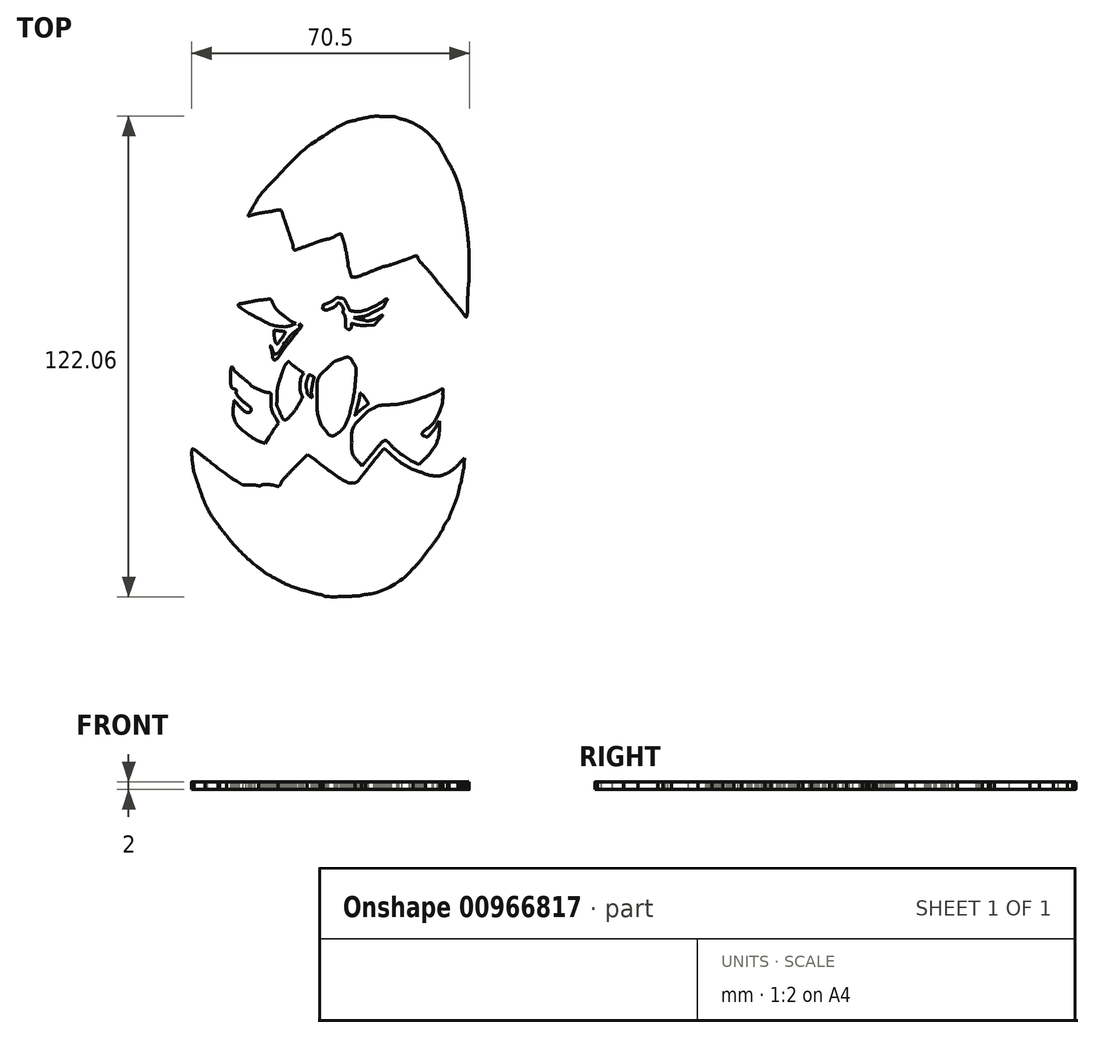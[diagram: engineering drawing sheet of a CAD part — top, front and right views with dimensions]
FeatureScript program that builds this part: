
annotation { "Feature Type Name" : "Feature", "Feature Type Description" : "" }
export const myFeature = defineFeature(function(context is Context, id is Id, definition is map)
    precondition{}
    {
        {
            var Q0;
            Q0=qCreatedBy(makeId("Top.planeOp"),FACE);
            var sketch = newSketch(context, id + "F0", { "sketchPlane" : qUnion([Q0])});
            skLineSegment(sketch, "E0", {"start": v(-17.46, -21.76) * mm, "end": v(-17.2, -21.16) * mm});
            skLineSegment(sketch, "E1", {"start": v(-17.2, -21.16) * mm, "end": v(-18.13, -20.78) * mm});
            skLineSegment(sketch, "E2", {"start": v(-18.45, 30) * mm, "end": v(-17.65, 29.34) * mm});
            skLineSegment(sketch, "E3", {"start": v(-17.65, 29.34) * mm, "end": v(-16.71, 30.75) * mm});
            skLineSegment(sketch, "E4", {"start": v(1.27, -59.92) * mm, "end": v(1.27, -59.92) * mm});
            skLineSegment(sketch, "E5", {"start": v(34.2, -24.61) * mm, "end": v(34.3, -23.27) * mm});
            skLineSegment(sketch, "E6", {"start": v(34.3, -23.27) * mm, "end": v(33.3, -24.29) * mm});
            skLineSegment(sketch, "E7", {"start": v(-3.64, -23.79) * mm, "end": v(-5.61, -22.3) * mm});
            skLineSegment(sketch, "E8", {"start": v(-5.61, -22.3) * mm, "end": v(-8.8, -25.56) * mm});
            skLineSegment(sketch, "E9", {"start": v(-20.36, -30.12) * mm, "end": v(-22.08, -30.1) * mm});
            skLineSegment(sketch, "E10", {"start": v(-22.08, -30.1) * mm, "end": v(-23.62, -29.13) * mm});
            skLineSegment(sketch, "E11", {"start": v(-17.15, -27.15) * mm, "end": v(-17.23, -28.47) * mm});
            skLineSegment(sketch, "E12", {"start": v(-17.23, -28.47) * mm, "end": v(-16.05, -28.52) * mm});
            skLineSegment(sketch, "E13", {"start": v(22.12, -24.58) * mm, "end": v(22.75, -24.87) * mm});
            skLineSegment(sketch, "E14", {"start": v(22.75, -24.87) * mm, "end": v(24.01, -23.63) * mm});
            skLineSegment(sketch, "E15", {"start": v(27.87, -15.36) * mm, "end": v(27.96, -13.82) * mm});
            skLineSegment(sketch, "E16", {"start": v(27.96, -13.82) * mm, "end": v(27.27, -14.85) * mm});
            skLineSegment(sketch, "E17", {"start": v(7.53, -24.44) * mm, "end": v(8.27, -25.28) * mm});
            skLineSegment(sketch, "E18", {"start": v(8.27, -25.28) * mm, "end": v(8.8, -24.62) * mm});
            skLineSegment(sketch, "E19", {"start": v(-13.66, -15.29) * mm, "end": v(-12.95, -14.31) * mm});
            skLineSegment(sketch, "E20", {"start": v(-12.95, -14.31) * mm, "end": v(-13.44, -13.47) * mm});
            skLineSegment(sketch, "E21", {"start": v(-17.02, -19.32) * mm, "end": v(-16.43, -19.53) * mm});
            skLineSegment(sketch, "E22", {"start": v(-16.43, -19.53) * mm, "end": v(-15.4, -17.9) * mm});
            skLineSegment(sketch, "E23", {"start": v(-6.81, -2.07) * mm, "end": v(-6.57, -1.6) * mm});
            skLineSegment(sketch, "E24", {"start": v(-6.57, -1.6) * mm, "end": v(-7.92, -0.7) * mm});
            skLineSegment(sketch, "E25", {"start": v(29.38, 15.62) * mm, "end": v(29.62, 16.5) * mm});
            skLineSegment(sketch, "E26", {"start": v(29.62, 16.5) * mm, "end": v(28.6, 17.81) * mm});
            skLineSegment(sketch, "E27", {"start": v(2.14, 31.23) * mm, "end": v(1.95, 31.69) * mm});
            skLineSegment(sketch, "E28", {"start": v(1.95, 31.69) * mm, "end": v(1.17, 31.38) * mm});
            skLineSegment(sketch, "E29", {"start": v(-14.7, 31.12) * mm, "end": v(-15.85, 29.58) * mm});
            skLineSegment(sketch, "E30", {"start": v(-15.85, 29.58) * mm, "end": v(-15.28, 29.52) * mm});
            skLineSegment(sketch, "E31", {"start": v(-4.13, -0.77) * mm, "end": v(-3.33, -1.07) * mm});
            skLineSegment(sketch, "E32", {"start": v(-3.33, -1.07) * mm, "end": v(-1.73, 0.55) * mm});
            skLineSegment(sketch, "E33", {"start": v(10.62, -1.64) * mm, "end": v(10.62, -1.64) * mm});
            skLineSegment(sketch, "E34", {"start": v(7.22, 12.57) * mm, "end": v(6.1, 12.46) * mm});
            skLineSegment(sketch, "E35", {"start": v(6.1, 12.46) * mm, "end": v(6.76, 12.23) * mm});
            skLineSegment(sketch, "E36", {"start": v(11.8, 11.02) * mm, "end": v(11.39, 10.49) * mm});
            skLineSegment(sketch, "E37", {"start": v(11.39, 10.49) * mm, "end": v(9.4, 10.47) * mm});
            skLineSegment(sketch, "E38", {"start": v(-9.31, 10.68) * mm, "end": v(-8.56, 10.9) * mm});
            skLineSegment(sketch, "E39", {"start": v(-8.56, 10.9) * mm, "end": v(-9.36, 11.3) * mm});
            skFitSpline(sketch, "E40", {"points": [v(1.27, -59.92) * mm, v(1.26, -59.9) * mm, v(0.65, -59.88) * mm, v(-0.08, -59.86) * mm]});
            skFitSpline(sketch, "E41", {"points": [v(-0.08, -59.86) * mm, v(-1.27, -59.82) * mm, v(-3.66, -59.47) * mm, v(-3.97, -59.28) * mm]});
            skFitSpline(sketch, "E42", {"points": [v(-3.97, -59.28) * mm, v(-4.04, -59.24) * mm, v(-4.28, -59.17) * mm, v(-4.5, -59.13) * mm]});
            skFitSpline(sketch, "E43", {"points": [v(-4.5, -59.13) * mm, v(-4.74, -59.08) * mm, v(-5.43, -58.89) * mm, v(-6.04, -58.69) * mm]});
            skFitSpline(sketch, "E44", {"points": [v(-6.04, -58.69) * mm, v(-6.66, -58.49) * mm, v(-7.34, -58.29) * mm, v(-7.55, -58.25) * mm]});
            skFitSpline(sketch, "E45", {"points": [v(-7.55, -58.25) * mm, v(-7.95, -58.17) * mm, v(-9.79, -57.56) * mm, v(-10.41, -57.3) * mm]});
            skFitSpline(sketch, "E46", {"points": [v(-10.41, -57.3) * mm, v(-10.6, -57.23) * mm, v(-11.03, -57.06) * mm, v(-11.36, -56.95) * mm]});
            skFitSpline(sketch, "E47", {"points": [v(-11.36, -56.95) * mm, v(-12.67, -56.48) * mm, v(-16.33, -54.48) * mm, v(-17.73, -53.48) * mm]});
            skFitSpline(sketch, "E48", {"points": [v(-17.73, -53.48) * mm, v(-19.95, -51.87) * mm, v(-20.39, -51.49) * mm, v(-23.53, -48.3) * mm]});
            skFitSpline(sketch, "E49", {"points": [v(-23.53, -48.3) * mm, v(-26.57, -45.24) * mm, v(-27.3, -44.44) * mm, v(-27.3, -44.2) * mm]});
            skFitSpline(sketch, "E50", {"points": [v(-27.3, -44.2) * mm, v(-27.3, -44.13) * mm, v(-27.69, -43.67) * mm, v(-28.15, -43.18) * mm]});
            skFitSpline(sketch, "E51", {"points": [v(-28.15, -43.18) * mm, v(-29.6, -41.64) * mm, v(-32.25, -37.44) * mm, v(-33.3, -35) * mm]});
            skFitSpline(sketch, "E52", {"points": [v(-33.3, -35) * mm, v(-33.74, -33.98) * mm, v(-34.5, -31.98) * mm, v(-34.6, -31.57) * mm]});
            skFitSpline(sketch, "E53", {"points": [v(-34.6, -31.57) * mm, v(-34.63, -31.43) * mm, v(-34.87, -30.73) * mm, v(-35.12, -30.03) * mm]});
            skFitSpline(sketch, "E54", {"points": [v(-35.12, -30.03) * mm, v(-36.14, -27.15) * mm, v(-36.31, -26.07) * mm, v(-36.31, -22.74) * mm]});
            skFitSpline(sketch, "E55", {"points": [v(-36.31, -22.74) * mm, v(-36.31, -19.95) * mm, v(-36.16, -18.7) * mm, v(-35.78, -18.41) * mm]});
            skFitSpline(sketch, "E56", {"points": [v(-35.78, -18.41) * mm, v(-35.35, -18.1) * mm, v(-35.24, -18.13) * mm, v(-34.72, -18.68) * mm]});
            skFitSpline(sketch, "E57", {"points": [v(-34.72, -18.68) * mm, v(-34.46, -18.94) * mm, v(-33.4, -19.8) * mm, v(-32.37, -20.6) * mm]});
            skFitSpline(sketch, "E58", {"points": [v(-32.37, -20.6) * mm, v(-31.33, -21.4) * mm, v(-30.44, -22.08) * mm, v(-30.4, -22.13) * mm]});
            skFitSpline(sketch, "E59", {"points": [v(-30.4, -22.13) * mm, v(-30.35, -22.18) * mm, v(-30, -22.45) * mm, v(-29.62, -22.73) * mm]});
            skFitSpline(sketch, "E60", {"points": [v(-29.62, -22.73) * mm, v(-29.25, -23) * mm, v(-28.9, -23.28) * mm, v(-28.85, -23.34) * mm]});
            skFitSpline(sketch, "E61", {"points": [v(-28.85, -23.34) * mm, v(-28.5, -23.78) * mm, v(-24.34, -26.7) * mm, v(-21.83, -28.27) * mm]});
            skFitSpline(sketch, "E62", {"points": [v(-21.83, -28.27) * mm, v(-21.4, -28.54) * mm, v(-18.97, -28.72) * mm, v(-18.83, -28.5) * mm]});
            skFitSpline(sketch, "E63", {"points": [v(-18.83, -28.5) * mm, v(-18.8, -28.44) * mm, v(-18.71, -27.85) * mm, v(-18.66, -27.2) * mm]});
            skFitSpline(sketch, "E64", {"points": [v(-18.66, -27.2) * mm, v(-18.6, -26.53) * mm, v(-18.52, -25.88) * mm, v(-18.48, -25.74) * mm]});
            skFitSpline(sketch, "E65", {"points": [v(-18.48, -25.74) * mm, v(-18.44, -25.6) * mm, v(-18.36, -25.21) * mm, v(-18.3, -24.88) * mm]});
            skFitSpline(sketch, "E66", {"points": [v(-18.3, -24.88) * mm, v(-18.15, -23.95) * mm, v(-17.73, -22.42) * mm, v(-17.46, -21.76) * mm]});
            skFitSpline(sketch, "E67", {"points": [v(-18.13, -20.78) * mm, v(-19.25, -20.32) * mm, v(-21.1, -19.04) * mm, v(-22.2, -17.97) * mm]});
            skFitSpline(sketch, "E68", {"points": [v(-22.2, -17.97) * mm, v(-24.52, -15.7) * mm, v(-25.92, -12.27) * mm, v(-25.71, -9.36) * mm]});
            skFitSpline(sketch, "E69", {"points": [v(-25.71, -9.36) * mm, v(-25.66, -8.6) * mm, v(-25.57, -7.8) * mm, v(-25.52, -7.56) * mm]});
            skFitSpline(sketch, "E70", {"points": [v(-25.52, -7.56) * mm, v(-25.45, -7.28) * mm, v(-25.58, -6.8) * mm, v(-25.9, -6.19) * mm]});
            skFitSpline(sketch, "E71", {"points": [v(-25.9, -6.19) * mm, v(-26.36, -5.26) * mm, v(-26.36, -5.19) * mm, v(-26.34, -2.4) * mm]});
            skFitSpline(sketch, "E72", {"points": [v(-26.34, -2.4) * mm, v(-26.32, 0.35) * mm, v(-26.3, 0.5) * mm, v(-25.83, 1.5) * mm]});
            skFitSpline(sketch, "E73", {"points": [v(-25.83, 1.5) * mm, v(-25.31, 2.6) * mm, v(-25.08, 2.81) * mm, v(-24.52, 2.63) * mm]});
            skFitSpline(sketch, "E74", {"points": [v(-24.52, 2.63) * mm, v(-24.2, 2.53) * mm, v(-23.26, 0.76) * mm, v(-23.35, 0.42) * mm]});
            skFitSpline(sketch, "E75", {"points": [v(-23.35, 0.42) * mm, v(-23.37, 0.32) * mm, v(-23.34, 0.3) * mm, v(-23.28, 0.36) * mm]});
            skFitSpline(sketch, "E76", {"points": [v(-23.28, 0.36) * mm, v(-23.21, 0.43) * mm, v(-22.92, 0.2) * mm, v(-22.62, -0.15) * mm]});
            skFitSpline(sketch, "E77", {"points": [v(-22.62, -0.15) * mm, v(-21.35, -1.63) * mm, v(-19.86, -2.83) * mm, v(-18.05, -3.82) * mm]});
            skFitSpline(sketch, "E78", {"points": [v(-18.05, -3.82) * mm, v(-16.84, -4.48) * mm, v(-14.67, -5.27) * mm, v(-14.5, -5.1) * mm]});
            skFitSpline(sketch, "E79", {"points": [v(-14.5, -5.1) * mm, v(-14.45, -5.05) * mm, v(-14.34, -4.64) * mm, v(-14.25, -4.2) * mm]});
            skFitSpline(sketch, "E80", {"points": [v(-14.25, -4.2) * mm, v(-14.17, -3.75) * mm, v(-13.8, -2.54) * mm, v(-13.42, -1.51) * mm]});
            skFitSpline(sketch, "E81", {"points": [v(-13.42, -1.51) * mm, v(-13.04, -0.48) * mm, v(-12.73, 0.4) * mm, v(-12.73, 0.44) * mm]});
            skFitSpline(sketch, "E82", {"points": [v(-12.73, 0.44) * mm, v(-12.73, 0.48) * mm, v(-12.88, 0.44) * mm, v(-13.06, 0.34) * mm]});
            skFitSpline(sketch, "E83", {"points": [v(-13.06, 0.34) * mm, v(-13.52, 0.1) * mm, v(-14.64, 0.13) * mm, v(-15, 0.4) * mm]});
            skFitSpline(sketch, "E84", {"points": [v(-15, 0.4) * mm, v(-15.38, 0.69) * mm, v(-15.76, 1.59) * mm, v(-15.9, 2.56) * mm]});
            skFitSpline(sketch, "E85", {"points": [v(-15.9, 2.56) * mm, v(-15.96, 2.98) * mm, v(-16.08, 3.44) * mm, v(-16.15, 3.58) * mm]});
            skFitSpline(sketch, "E86", {"points": [v(-16.15, 3.58) * mm, v(-16.27, 3.82) * mm, v(-16.4, 4.35) * mm, v(-16.62, 5.56) * mm]});
            skFitSpline(sketch, "E87", {"points": [v(-16.62, 5.56) * mm, v(-16.66, 5.75) * mm, v(-16.76, 6.18) * mm, v(-16.84, 6.5) * mm]});
            skFitSpline(sketch, "E88", {"points": [v(-16.84, 6.5) * mm, v(-16.93, 6.84) * mm, v(-17.05, 7.5) * mm, v(-17.1, 7.96) * mm]});
            skFitSpline(sketch, "E89", {"points": [v(-17.1, 7.96) * mm, v(-17.34, 10) * mm, v(-17.42, 10.14) * mm, v(-18.96, 10.96) * mm]});
            skFitSpline(sketch, "E90", {"points": [v(-18.96, 10.96) * mm, v(-21.2, 12.16) * mm, v(-22.57, 13.1) * mm, v(-23.47, 14.06) * mm]});
            skFitSpline(sketch, "E91", {"points": [v(-23.47, 14.06) * mm, v(-23.93, 14.55) * mm, v(-24.56, 15.19) * mm, v(-24.86, 15.48) * mm]});
            skFitSpline(sketch, "E92", {"points": [v(-24.86, 15.48) * mm, v(-25.4, 16) * mm, v(-25.55, 16.5) * mm, v(-25.28, 16.93) * mm]});
            skFitSpline(sketch, "E93", {"points": [v(-25.28, 16.93) * mm, v(-25.2, 17.05) * mm, v(-24.5, 17.22) * mm, v(-23.7, 17.31) * mm]});
            skFitSpline(sketch, "E94", {"points": [v(-23.7, 17.31) * mm, v(-20.78, 17.66) * mm, v(-20.15, 17.79) * mm, v(-19.98, 18.06) * mm]});
            skFitSpline(sketch, "E95", {"points": [v(-19.98, 18.06) * mm, v(-19.91, 18.17) * mm, v(-19.85, 19.03) * mm, v(-19.84, 19.97) * mm]});
            skFitSpline(sketch, "E96", {"points": [v(-19.84, 19.97) * mm, v(-19.83, 20.91) * mm, v(-19.76, 22) * mm, v(-19.68, 22.37) * mm]});
            skFitSpline(sketch, "E97", {"points": [v(-19.68, 22.37) * mm, v(-19.52, 23.17) * mm, v(-19.47, 23.5) * mm, v(-19.34, 24.38) * mm]});
            skFitSpline(sketch, "E98", {"points": [v(-19.34, 24.38) * mm, v(-19.29, 24.74) * mm, v(-19.09, 25.42) * mm, v(-18.9, 25.9) * mm]});
            skFitSpline(sketch, "E99", {"points": [v(-18.9, 25.9) * mm, v(-18.7, 26.4) * mm, v(-18.58, 26.82) * mm, v(-18.62, 26.86) * mm]});
            skFitSpline(sketch, "E100", {"points": [v(-18.62, 26.86) * mm, v(-18.66, 26.9) * mm, v(-18.87, 26.96) * mm, v(-19.1, 27) * mm]});
            skFitSpline(sketch, "E101", {"points": [v(-19.1, 27) * mm, v(-20.3, 27.23) * mm, v(-20.6, 27.3) * mm, v(-21.36, 27.55) * mm]});
            skFitSpline(sketch, "E102", {"points": [v(-21.36, 27.55) * mm, v(-22.16, 27.8) * mm, v(-22.18, 27.82) * mm, v(-22.13, 28.43) * mm]});
            skFitSpline(sketch, "E103", {"points": [v(-22.13, 28.43) * mm, v(-22.08, 28.98) * mm, v(-22.02, 29.06) * mm, v(-21.65, 29.06) * mm]});
            skFitSpline(sketch, "E104", {"points": [v(-21.65, 29.06) * mm, v(-21.41, 29.06) * mm, v(-20.85, 28.95) * mm, v(-20.4, 28.82) * mm]});
            skFitSpline(sketch, "E105", {"points": [v(-20.4, 28.82) * mm, v(-19.47, 28.55) * mm, v(-19.2, 28.66) * mm, v(-19.7, 29.1) * mm]});
            skFitSpline(sketch, "E106", {"points": [v(-19.7, 29.1) * mm, v(-20.3, 29.62) * mm, v(-21.3, 31.05) * mm, v(-21.3, 31.36) * mm]});
            skFitSpline(sketch, "E107", {"points": [v(-21.3, 31.36) * mm, v(-21.3, 31.52) * mm, v(-21.2, 31.8) * mm, v(-21.06, 31.99) * mm]});
            skFitSpline(sketch, "E108", {"points": [v(-21.06, 31.99) * mm, v(-20.82, 32.3) * mm, v(-20.77, 32.29) * mm, v(-20.02, 31.49) * mm]});
            skFitSpline(sketch, "E109", {"points": [v(-20.02, 31.49) * mm, v(-19.6, 31.03) * mm, v(-18.88, 30.36) * mm, v(-18.45, 30) * mm]});
            skFitSpline(sketch, "E110", {"points": [v(-16.71, 30.75) * mm, v(-15.72, 32.22) * mm, v(-14.5, 33.72) * mm, v(-13.29, 34.94) * mm]});
            skFitSpline(sketch, "E111", {"points": [v(-13.29, 34.94) * mm, v(-12.89, 35.35) * mm, v(-12.56, 35.78) * mm, v(-12.56, 35.9) * mm]});
            skFitSpline(sketch, "E112", {"points": [v(-12.56, 35.9) * mm, v(-12.56, 36.03) * mm, v(-12.75, 36.58) * mm, v(-13, 37.12) * mm]});
            skFitSpline(sketch, "E113", {"points": [v(-13, 37.12) * mm, v(-13.41, 38.07) * mm, v(-13.44, 38.1) * mm, v(-13.98, 38) * mm]});
            skFitSpline(sketch, "E114", {"points": [v(-13.98, 38) * mm, v(-14.28, 37.94) * mm, v(-14.88, 37.85) * mm, v(-15.3, 37.8) * mm]});
            skFitSpline(sketch, "E115", {"points": [v(-15.3, 37.8) * mm, v(-16.83, 37.6) * mm, v(-18.84, 37.22) * mm, v(-19.68, 36.97) * mm]});
            skFitSpline(sketch, "E116", {"points": [v(-19.68, 36.97) * mm, v(-20.15, 36.83) * mm, v(-20.8, 36.68) * mm, v(-21.11, 36.63) * mm]});
            skFitSpline(sketch, "E117", {"points": [v(-21.11, 36.63) * mm, v(-21.43, 36.58) * mm, v(-21.78, 36.46) * mm, v(-21.88, 36.36) * mm]});
            skFitSpline(sketch, "E118", {"points": [v(-21.88, 36.36) * mm, v(-21.98, 36.26) * mm, v(-22.23, 36.18) * mm, v(-22.43, 36.18) * mm]});
            skFitSpline(sketch, "E119", {"points": [v(-22.43, 36.18) * mm, v(-23.27, 36.18) * mm, v(-23.33, 37.1) * mm, v(-22.58, 38.3) * mm]});
            skFitSpline(sketch, "E120", {"points": [v(-22.58, 38.3) * mm, v(-18.92, 44.18) * mm, v(-17.85, 45.64) * mm, v(-15.56, 47.93) * mm]});
            skFitSpline(sketch, "E121", {"points": [v(-15.56, 47.93) * mm, v(-11.69, 51.78) * mm, v(-7.49, 55.82) * mm, v(-6.47, 56.68) * mm]});
            skFitSpline(sketch, "E122", {"points": [v(-6.47, 56.68) * mm, v(-5.9, 57.15) * mm, v(-5.3, 57.67) * mm, v(-5.11, 57.83) * mm]});
            skFitSpline(sketch, "E123", {"points": [v(-5.11, 57.83) * mm, v(-4.93, 58) * mm, v(-4.47, 58.34) * mm, v(-4.08, 58.6) * mm]});
            skFitSpline(sketch, "E124", {"points": [v(-4.08, 58.6) * mm, v(-3.7, 58.86) * mm, v(-3.34, 59.12) * mm, v(-3.3, 59.17) * mm]});
            skFitSpline(sketch, "E125", {"points": [v(-3.3, 59.17) * mm, v(-3, 59.52) * mm, v(-0.76, 60.87) * mm, v(1.19, 61.9) * mm]});
            skFitSpline(sketch, "E126", {"points": [v(1.19, 61.9) * mm, v(3.19, 62.94) * mm, v(6.18, 64.11) * mm, v(7.5, 64.37) * mm]});
            skFitSpline(sketch, "E127", {"points": [v(7.5, 64.37) * mm, v(10.28, 64.92) * mm, v(11.13, 65.02) * mm, v(13.51, 65.08) * mm]});
            skFitSpline(sketch, "E128", {"points": [v(13.51, 65.08) * mm, v(16.1, 65.14) * mm, v(17.32, 64.98) * mm, v(19.28, 64.32) * mm]});
            skFitSpline(sketch, "E129", {"points": [v(19.28, 64.32) * mm, v(22.87, 63.12) * mm, v(26.24, 60.84) * mm, v(28.16, 58.32) * mm]});
            skFitSpline(sketch, "E130", {"points": [v(28.16, 58.32) * mm, v(29.25, 56.9) * mm, v(30.5, 54.73) * mm, v(31.9, 51.86) * mm]});
            skFitSpline(sketch, "E131", {"points": [v(31.9, 51.86) * mm, v(33.32, 48.96) * mm, v(33.81, 47.6) * mm, v(34.7, 44.15) * mm]});
            skFitSpline(sketch, "E132", {"points": [v(34.7, 44.15) * mm, v(35.4, 41.35) * mm, v(35.4, 41.33) * mm, v(35.72, 39) * mm]});
            skFitSpline(sketch, "E133", {"points": [v(35.72, 39) * mm, v(35.76, 38.73) * mm, v(35.83, 38.34) * mm, v(35.87, 38.15) * mm]});
            skFitSpline(sketch, "E134", {"points": [v(35.87, 38.15) * mm, v(35.91, 37.96) * mm, v(36, 37.23) * mm, v(36.06, 36.52) * mm]});
            skFitSpline(sketch, "E135", {"points": [v(36.06, 36.52) * mm, v(36.12, 35.81) * mm, v(36.2, 35.04) * mm, v(36.24, 34.8) * mm]});
            skFitSpline(sketch, "E136", {"points": [v(36.24, 34.8) * mm, v(36.42, 33.5) * mm, v(36.54, 32.41) * mm, v(36.6, 31.64) * mm]});
            skFitSpline(sketch, "E137", {"points": [v(36.6, 31.64) * mm, v(36.7, 30.29) * mm, v(36.68, 21.7) * mm, v(36.58, 19.8) * mm]});
            skFitSpline(sketch, "E138", {"points": [v(36.58, 19.8) * mm, v(36.53, 18.86) * mm, v(36.46, 17.12) * mm, v(36.42, 15.94) * mm]});
            skFitSpline(sketch, "E139", {"points": [v(36.42, 15.94) * mm, v(36.39, 14.76) * mm, v(36.32, 13.53) * mm, v(36.27, 13.2) * mm]});
            skFitSpline(sketch, "E140", {"points": [v(36.27, 13.2) * mm, v(36.22, 12.87) * mm, v(36.15, 12) * mm, v(36.13, 11.27) * mm]});
            skFitSpline(sketch, "E141", {"points": [v(36.13, 11.27) * mm, v(36.08, 9.8) * mm, v(35.94, 9.62) * mm, v(34.96, 9.74) * mm]});
            skFitSpline(sketch, "E142", {"points": [v(34.96, 9.74) * mm, v(34.87, 9.76) * mm, v(34.55, 10.13) * mm, v(34.24, 10.58) * mm]});
            skFitSpline(sketch, "E143", {"points": [v(34.24, 10.58) * mm, v(33.3, 11.98) * mm, v(31.15, 14.65) * mm, v(30.94, 14.69) * mm]});
            skFitSpline(sketch, "E144", {"points": [v(30.94, 14.69) * mm, v(30.84, 14.7) * mm, v(30.45, 14.1) * mm, v(30.08, 13.33) * mm]});
            skFitSpline(sketch, "E145", {"points": [v(30.08, 13.33) * mm, v(29.52, 12.15) * mm, v(27.77, 9.36) * mm, v(27.43, 9.08) * mm]});
            skFitSpline(sketch, "E146", {"points": [v(27.43, 9.08) * mm, v(27.37, 9.03) * mm, v(27.05, 8.65) * mm, v(26.72, 8.22) * mm]});
            skFitSpline(sketch, "E147", {"points": [v(26.72, 8.22) * mm, v(25.14, 6.17) * mm, v(22.07, 3.18) * mm, v(19.77, 1.46) * mm]});
            skFitSpline(sketch, "E148", {"points": [v(19.77, 1.46) * mm, v(15.83, -1.5) * mm, v(12.7, -2.94) * mm, v(9, -3.51) * mm]});
            skFitSpline(sketch, "E149", {"points": [v(9, -3.51) * mm, v(8.15, -3.65) * mm, v(8.08, -3.7) * mm, v(7.99, -4.2) * mm]});
            skFitSpline(sketch, "E150", {"points": [v(7.99, -4.2) * mm, v(7.92, -4.52) * mm, v(8.1, -4.8) * mm, v(8.83, -5.52) * mm]});
            skFitSpline(sketch, "E151", {"points": [v(8.83, -5.52) * mm, v(9.35, -6.02) * mm, v(10.11, -6.96) * mm, v(10.54, -7.6) * mm]});
            skFitSpline(sketch, "E152", {"points": [v(10.54, -7.6) * mm, v(11.37, -8.85) * mm, v(11.31, -8.83) * mm, v(12.65, -8.53) * mm]});
            skFitSpline(sketch, "E153", {"points": [v(12.65, -8.53) * mm, v(12.9, -8.48) * mm, v(13.9, -8.39) * mm, v(14.88, -8.33) * mm]});
            skFitSpline(sketch, "E154", {"points": [v(14.88, -8.33) * mm, v(15.88, -8.28) * mm, v(16.88, -8.2) * mm, v(17.11, -8.18) * mm]});
            skFitSpline(sketch, "E155", {"points": [v(17.11, -8.18) * mm, v(18.52, -7.98) * mm, v(19.3, -7.84) * mm, v(19.69, -7.7) * mm]});
            skFitSpline(sketch, "E156", {"points": [v(19.69, -7.7) * mm, v(19.92, -7.6) * mm, v(20.23, -7.5) * mm, v(20.37, -7.47) * mm]});
            skFitSpline(sketch, "E157", {"points": [v(20.37, -7.47) * mm, v(20.85, -7.37) * mm, v(24.4, -6.07) * mm, v(25.7, -5.53) * mm]});
            skFitSpline(sketch, "E158", {"points": [v(25.7, -5.53) * mm, v(26.4, -5.23) * mm, v(27.5, -4.64) * mm, v(28.15, -4.23) * mm]});
            skFitSpline(sketch, "E159", {"points": [v(28.15, -4.23) * mm, v(29.18, -3.56) * mm, v(29.38, -3.49) * mm, v(29.74, -3.65) * mm]});
            skFitSpline(sketch, "E160", {"points": [v(29.74, -3.65) * mm, v(30.29, -3.9) * mm, v(30.38, -4.36) * mm, v(30.28, -6.16) * mm]});
            skFitSpline(sketch, "E161", {"points": [v(30.28, -6.16) * mm, v(30.18, -7.86) * mm, v(30.24, -7.56) * mm, v(29.46, -9.97) * mm]});
            skFitSpline(sketch, "E162", {"points": [v(29.46, -9.97) * mm, v(29.05, -11.2) * mm, v(28.9, -11.95) * mm, v(28.98, -12.18) * mm]});
            skFitSpline(sketch, "E163", {"points": [v(28.98, -12.18) * mm, v(29.42, -13.38) * mm, v(29.45, -15.77) * mm, v(29.04, -17.28) * mm]});
            skFitSpline(sketch, "E164", {"points": [v(29.04, -17.28) * mm, v(28.89, -17.83) * mm, v(28.72, -18.47) * mm, v(28.68, -18.7) * mm]});
            skFitSpline(sketch, "E165", {"points": [v(28.68, -18.7) * mm, v(28.53, -19.45) * mm, v(27.12, -22.2) * mm, v(26.4, -23.17) * mm]});
            skFitSpline(sketch, "E166", {"points": [v(26.4, -23.17) * mm, v(26.01, -23.67) * mm, v(25.42, -24.39) * mm, v(25.07, -24.75) * mm]});
            skFitSpline(sketch, "E167", {"points": [v(25.07, -24.75) * mm, v(24.73, -25.11) * mm, v(24.48, -25.43) * mm, v(24.51, -25.46) * mm]});
            skFitSpline(sketch, "E168", {"points": [v(24.51, -25.46) * mm, v(24.81, -25.71) * mm, v(25.92, -25.88) * mm, v(27.21, -25.87) * mm]});
            skFitSpline(sketch, "E169", {"points": [v(27.21, -25.87) * mm, v(28.58, -25.87) * mm, v(28.84, -25.81) * mm, v(29.41, -25.43) * mm]});
            skFitSpline(sketch, "E170", {"points": [v(29.41, -25.43) * mm, v(29.77, -25.19) * mm, v(30.1, -24.94) * mm, v(30.15, -24.88) * mm]});
            skFitSpline(sketch, "E171", {"points": [v(30.15, -24.88) * mm, v(30.2, -24.82) * mm, v(30.58, -24.53) * mm, v(31, -24.24) * mm]});
            skFitSpline(sketch, "E172", {"points": [v(31, -24.24) * mm, v(31.8, -23.7) * mm, v(32.27, -23.28) * mm, v(32.72, -22.72) * mm]});
            skFitSpline(sketch, "E173", {"points": [v(32.72, -22.72) * mm, v(34.19, -20.89) * mm, v(34.32, -20.76) * mm, v(34.8, -20.76) * mm]});
            skFitSpline(sketch, "E174", {"points": [v(34.8, -20.76) * mm, v(35.56, -20.76) * mm, v(35.79, -21.26) * mm, v(35.72, -22.8) * mm]});
            skFitSpline(sketch, "E175", {"points": [v(35.72, -22.8) * mm, v(35.63, -24.68) * mm, v(35.46, -26.82) * mm, v(35.38, -27.3) * mm]});
            skFitSpline(sketch, "E176", {"points": [v(35.38, -27.3) * mm, v(35.13, -28.7) * mm, v(34.36, -31.87) * mm, v(33.97, -33.11) * mm]});
            skFitSpline(sketch, "E177", {"points": [v(33.97, -33.11) * mm, v(33.72, -33.92) * mm, v(33.5, -34.61) * mm, v(33.5, -34.66) * mm]});
            skFitSpline(sketch, "E178", {"points": [v(33.5, -34.66) * mm, v(33.45, -34.78) * mm, v(33.3, -35.13) * mm, v(32.37, -37.4) * mm]});
            skFitSpline(sketch, "E179", {"points": [v(32.37, -37.4) * mm, v(30.8, -41.16) * mm, v(29, -44.06) * mm, v(24.83, -49.58) * mm]});
            skFitSpline(sketch, "E180", {"points": [v(24.83, -49.58) * mm, v(22.9, -52.13) * mm, v(19.37, -55.07) * mm, v(16.35, -56.64) * mm]});
            skFitSpline(sketch, "E181", {"points": [v(16.35, -56.64) * mm, v(15.78, -56.93) * mm, v(15.12, -57.31) * mm, v(14.89, -57.48) * mm]});
            skFitSpline(sketch, "E182", {"points": [v(14.89, -57.48) * mm, v(14.14, -58.02) * mm, v(10.72, -59.2) * mm, v(9.22, -59.44) * mm]});
            skFitSpline(sketch, "E183", {"points": [v(9.22, -59.44) * mm, v(8.9, -59.5) * mm, v(8.43, -59.57) * mm, v(8.2, -59.61) * mm]});
            skFitSpline(sketch, "E184", {"points": [v(8.2, -59.61) * mm, v(6.85, -59.86) * mm, v(5.98, -59.92) * mm, v(3.76, -59.94) * mm]});
            skFitSpline(sketch, "E185", {"points": [v(3.76, -59.94) * mm, v(2.41, -59.95) * mm, v(1.3, -59.94) * mm, v(1.27, -59.92) * mm]});
            skFitSpline(sketch, "E186", {"points": [v(6.48, -58.32) * mm, v(7.1, -58.3) * mm, v(7.83, -58.2) * mm, v(8.1, -58.13) * mm]});
            skFitSpline(sketch, "E187", {"points": [v(8.1, -58.13) * mm, v(8.4, -58.04) * mm, v(8.86, -57.94) * mm, v(9.14, -57.89) * mm]});
            skFitSpline(sketch, "E188", {"points": [v(9.14, -57.89) * mm, v(12.36, -57.3) * mm, v(18.47, -53.98) * mm, v(21.17, -51.34) * mm]});
            skFitSpline(sketch, "E189", {"points": [v(21.17, -51.34) * mm, v(22, -50.52) * mm, v(23.35, -48.93) * mm, v(24.33, -47.61) * mm]});
            skFitSpline(sketch, "E190", {"points": [v(24.33, -47.61) * mm, v(24.75, -47.05) * mm, v(25.18, -46.47) * mm, v(25.3, -46.32) * mm]});
            skFitSpline(sketch, "E191", {"points": [v(25.3, -46.32) * mm, v(26.2, -45.17) * mm, v(27.74, -43.04) * mm, v(28.01, -42.55) * mm]});
            skFitSpline(sketch, "E192", {"points": [v(28.01, -42.55) * mm, v(28.2, -42.22) * mm, v(28.44, -41.83) * mm, v(28.55, -41.69) * mm]});
            skFitSpline(sketch, "E193", {"points": [v(28.55, -41.69) * mm, v(28.66, -41.55) * mm, v(28.77, -41.36) * mm, v(28.78, -41.26) * mm]});
            skFitSpline(sketch, "E194", {"points": [v(28.78, -41.26) * mm, v(28.84, -40.94) * mm, v(29.5, -39.72) * mm, v(29.91, -39.17) * mm]});
            skFitSpline(sketch, "E195", {"points": [v(29.91, -39.17) * mm, v(30.14, -38.87) * mm, v(30.32, -38.57) * mm, v(30.32, -38.5) * mm]});
            skFitSpline(sketch, "E196", {"points": [v(30.32, -38.5) * mm, v(30.32, -38.45) * mm, v(30.82, -37.15) * mm, v(31.43, -35.63) * mm]});
            skFitSpline(sketch, "E197", {"points": [v(31.43, -35.63) * mm, v(32.03, -34.1) * mm, v(32.57, -32.66) * mm, v(32.62, -32.43) * mm]});
            skFitSpline(sketch, "E198", {"points": [v(32.62, -32.43) * mm, v(32.97, -30.79) * mm, v(33.2, -29.88) * mm, v(33.3, -29.73) * mm]});
            skFitSpline(sketch, "E199", {"points": [v(33.3, -29.73) * mm, v(33.35, -29.63) * mm, v(33.45, -29.25) * mm, v(33.5, -28.89) * mm]});
            skFitSpline(sketch, "E200", {"points": [v(33.5, -28.89) * mm, v(33.55, -28.52) * mm, v(33.63, -28.06) * mm, v(33.67, -27.87) * mm]});
            skFitSpline(sketch, "E201", {"points": [v(33.67, -27.87) * mm, v(33.71, -27.67) * mm, v(33.8, -27.2) * mm, v(33.85, -26.84) * mm]});
            skFitSpline(sketch, "E202", {"points": [v(33.85, -26.84) * mm, v(33.9, -26.47) * mm, v(33.99, -26.12) * mm, v(34.02, -26.06) * mm]});
            skFitSpline(sketch, "E203", {"points": [v(34.02, -26.06) * mm, v(34.05, -26) * mm, v(34.13, -25.36) * mm, v(34.2, -24.61) * mm]});
            skFitSpline(sketch, "E204", {"points": [v(33.3, -24.29) * mm, v(32.13, -25.48) * mm, v(30.36, -26.87) * mm, v(29.68, -27.13) * mm]});
            skFitSpline(sketch, "E205", {"points": [v(29.68, -27.13) * mm, v(28.11, -27.74) * mm, v(25.46, -27.62) * mm, v(23.15, -26.84) * mm]});
            skFitSpline(sketch, "E206", {"points": [v(23.15, -26.84) * mm, v(21, -26.1) * mm, v(17.05, -23.65) * mm, v(14.96, -21.75) * mm]});
            skFitSpline(sketch, "E207", {"points": [v(14.96, -21.75) * mm, v(14.47, -21.3) * mm, v(14, -20.94) * mm, v(13.91, -20.94) * mm]});
            skFitSpline(sketch, "E208", {"points": [v(13.91, -20.94) * mm, v(13.78, -20.94) * mm, v(13.19, -21.58) * mm, v(11.79, -23.24) * mm]});
            skFitSpline(sketch, "E209", {"points": [v(11.79, -23.24) * mm, v(11.55, -23.53) * mm, v(10.7, -24.62) * mm, v(9.9, -25.65) * mm]});
            skFitSpline(sketch, "E210", {"points": [v(9.9, -25.65) * mm, v(9.12, -26.7) * mm, v(8.42, -27.58) * mm, v(8.36, -27.63) * mm]});
            skFitSpline(sketch, "E211", {"points": [v(8.36, -27.63) * mm, v(8.3, -27.67) * mm, v(8.04, -28) * mm, v(7.77, -28.36) * mm]});
            skFitSpline(sketch, "E212", {"points": [v(7.77, -28.36) * mm, v(7.23, -29.09) * mm, v(6.54, -29.51) * mm, v(5.91, -29.51) * mm]});
            skFitSpline(sketch, "E213", {"points": [v(5.91, -29.51) * mm, v(4.86, -29.51) * mm, v(0.39, -26.83) * mm, v(-3.64, -23.79) * mm]});
            skFitSpline(sketch, "E214", {"points": [v(-8.8, -25.56) * mm, v(-10.57, -27.36) * mm, v(-12.13, -29.1) * mm, v(-12.29, -29.42) * mm]});
            skFitSpline(sketch, "E215", {"points": [v(-12.29, -29.42) * mm, v(-12.65, -30.18) * mm, v(-13.1, -30.43) * mm, v(-13.81, -30.26) * mm]});
            skFitSpline(sketch, "E216", {"points": [v(-13.81, -30.26) * mm, v(-14.62, -30.08) * mm, v(-17.24, -30.06) * mm, v(-17.49, -30.25) * mm]});
            skFitSpline(sketch, "E217", {"points": [v(-17.49, -30.25) * mm, v(-17.6, -30.34) * mm, v(-17.91, -30.35) * mm, v(-18.17, -30.27) * mm]});
            skFitSpline(sketch, "E218", {"points": [v(-18.17, -30.27) * mm, v(-18.43, -30.2) * mm, v(-19.42, -30.13) * mm, v(-20.36, -30.12) * mm]});
            skFitSpline(sketch, "E219", {"points": [v(-23.62, -29.13) * mm, v(-25.17, -28.16) * mm, v(-28, -26.1) * mm, v(-31.15, -23.62) * mm]});
            skFitSpline(sketch, "E220", {"points": [v(-31.15, -23.62) * mm, v(-33.57, -21.72) * mm, v(-34.8, -20.9) * mm, v(-34.9, -21.16) * mm]});
            skFitSpline(sketch, "E221", {"points": [v(-34.9, -21.16) * mm, v(-35, -21.48) * mm, v(-34.93, -23.64) * mm, v(-34.77, -24.97) * mm]});
            skFitSpline(sketch, "E222", {"points": [v(-34.77, -24.97) * mm, v(-34.68, -25.63) * mm, v(-34.6, -26.28) * mm, v(-34.6, -26.42) * mm]});
            skFitSpline(sketch, "E223", {"points": [v(-34.6, -26.42) * mm, v(-34.58, -26.57) * mm, v(-34.52, -26.8) * mm, v(-34.46, -26.94) * mm]});
            skFitSpline(sketch, "E224", {"points": [v(-34.46, -26.94) * mm, v(-34.4, -27.08) * mm, v(-33.85, -28.67) * mm, v(-33.24, -30.47) * mm]});
            skFitSpline(sketch, "E225", {"points": [v(-33.24, -30.47) * mm, v(-32.63, -32.27) * mm, v(-31.9, -34.26) * mm, v(-31.6, -34.9) * mm]});
            skFitSpline(sketch, "E226", {"points": [v(-31.6, -34.9) * mm, v(-31, -36.22) * mm, v(-29.26, -39.04) * mm, v(-28.4, -40.1) * mm]});
            skFitSpline(sketch, "E227", {"points": [v(-28.4, -40.1) * mm, v(-28.07, -40.5) * mm, v(-27.86, -40.83) * mm, v(-27.94, -40.83) * mm]});
            skFitSpline(sketch, "E228", {"points": [v(-27.94, -40.83) * mm, v(-28.02, -40.84) * mm, v(-28, -40.9) * mm, v(-27.9, -40.96) * mm]});
            skFitSpline(sketch, "E229", {"points": [v(-27.9, -40.96) * mm, v(-27.8, -41.03) * mm, v(-27.04, -41.94) * mm, v(-26.2, -42.98) * mm]});
            skFitSpline(sketch, "E230", {"points": [v(-26.2, -42.98) * mm, v(-24.18, -45.44) * mm, v(-20.3, -49.3) * mm, v(-18, -51.1) * mm]});
            skFitSpline(sketch, "E231", {"points": [v(-18, -51.1) * mm, v(-16.26, -52.47) * mm, v(-15.74, -52.8) * mm, v(-13.06, -54.24) * mm]});
            skFitSpline(sketch, "E232", {"points": [v(-13.06, -54.24) * mm, v(-11.43, -55.11) * mm, v(-7.77, -56.53) * mm, v(-5.78, -57.06) * mm]});
            skFitSpline(sketch, "E233", {"points": [v(-5.78, -57.06) * mm, v(-5.69, -57.08) * mm, v(-5.05, -57.26) * mm, v(-4.37, -57.46) * mm]});
            skFitSpline(sketch, "E234", {"points": [v(-4.37, -57.46) * mm, v(-3.68, -57.66) * mm, v(-2.83, -57.86) * mm, v(-2.48, -57.92) * mm]});
            skFitSpline(sketch, "E235", {"points": [v(-2.48, -57.92) * mm, v(-2.13, -57.97) * mm, v(-1.77, -58.06) * mm, v(-1.69, -58.1) * mm]});
            skFitSpline(sketch, "E236", {"points": [v(-1.69, -58.1) * mm, v(-1.31, -58.34) * mm, v(3.2, -58.46) * mm, v(6.48, -58.32) * mm]});
            skFitSpline(sketch, "E237", {"points": [v(-12.5, -27.26) * mm, v(-11.84, -26.57) * mm, v(-10.52, -25.18) * mm, v(-9.57, -24.19) * mm]});
            skFitSpline(sketch, "E238", {"points": [v(-9.57, -24.19) * mm, v(-8.62, -23.2) * mm, v(-7.37, -21.86) * mm, v(-6.79, -21.22) * mm]});
            skFitSpline(sketch, "E239", {"points": [v(-6.79, -21.22) * mm, v(-5.79, -20.12) * mm, v(-5.72, -20.08) * mm, v(-5.29, -20.27) * mm]});
            skFitSpline(sketch, "E240", {"points": [v(-5.29, -20.27) * mm, v(-5.04, -20.38) * mm, v(-4.84, -20.54) * mm, v(-4.84, -20.61) * mm]});
            skFitSpline(sketch, "E241", {"points": [v(-4.84, -20.61) * mm, v(-4.84, -20.68) * mm, v(-4.09, -21.3) * mm, v(-3.17, -22) * mm]});
            skFitSpline(sketch, "E242", {"points": [v(-3.17, -22) * mm, v(-2.25, -22.68) * mm, v(-1.46, -23.3) * mm, v(-1.4, -23.34) * mm]});
            skFitSpline(sketch, "E243", {"points": [v(-1.4, -23.34) * mm, v(-1.36, -23.4) * mm, v(-1.05, -23.63) * mm, v(-0.72, -23.85) * mm]});
            skFitSpline(sketch, "E244", {"points": [v(-0.72, -23.85) * mm, v(-0.4, -24.08) * mm, v(-0.08, -24.3) * mm, v(-0.04, -24.36) * mm]});
            skFitSpline(sketch, "E245", {"points": [v(-0.04, -24.36) * mm, v(0.35, -24.8) * mm, v(4.03, -26.97) * mm, v(5.32, -27.51) * mm]});
            skFitSpline(sketch, "E246", {"points": [v(5.32, -27.51) * mm, v(5.94, -27.77) * mm, v(5.98, -27.76) * mm, v(6.48, -27.34) * mm]});
            skFitSpline(sketch, "E247", {"points": [v(6.48, -27.34) * mm, v(6.76, -27.1) * mm, v(7, -26.83) * mm, v(7, -26.74) * mm]});
            skFitSpline(sketch, "E248", {"points": [v(7, -26.74) * mm, v(7, -26.64) * mm, v(6.7, -26.23) * mm, v(6.35, -25.83) * mm]});
            skFitSpline(sketch, "E249", {"points": [v(6.35, -25.83) * mm, v(6, -25.42) * mm, v(5.5, -24.68) * mm, v(5.24, -24.17) * mm]});
            skFitSpline(sketch, "E250", {"points": [v(5.24, -24.17) * mm, v(4.76, -23.24) * mm, v(4.21, -21.8) * mm, v(4.33, -21.8) * mm]});
            skFitSpline(sketch, "E251", {"points": [v(4.33, -21.8) * mm, v(4.37, -21.8) * mm, v(4.32, -21.54) * mm, v(4.23, -21.24) * mm]});
            skFitSpline(sketch, "E252", {"points": [v(4.23, -21.24) * mm, v(4.04, -20.6) * mm, v(4, -17.9) * mm, v(4.18, -17.4) * mm]});
            skFitSpline(sketch, "E253", {"points": [v(4.18, -17.4) * mm, v(4.26, -17.18) * mm, v(4.1, -17.27) * mm, v(3.63, -17.7) * mm]});
            skFitSpline(sketch, "E254", {"points": [v(3.63, -17.7) * mm, v(2.66, -18.6) * mm, v(2.37, -18.7) * mm, v(0.75, -18.7) * mm]});
            skFitSpline(sketch, "E255", {"points": [v(0.75, -18.7) * mm, v(-0.7, -18.7) * mm, v(-0.73, -18.7) * mm, v(-1.4, -18.1) * mm]});
            skFitSpline(sketch, "E256", {"points": [v(-1.4, -18.1) * mm, v(-1.77, -17.76) * mm, v(-2.3, -17) * mm, v(-2.6, -16.42) * mm]});
            skFitSpline(sketch, "E257", {"points": [v(-2.6, -16.42) * mm, v(-3.4, -14.82) * mm, v(-4.3, -11.87) * mm, v(-4.42, -10.45) * mm]});
            skFitSpline(sketch, "E258", {"points": [v(-4.42, -10.45) * mm, v(-4.48, -9.76) * mm, v(-4.6, -9.11) * mm, v(-4.69, -9.02) * mm]});
            skFitSpline(sketch, "E259", {"points": [v(-4.69, -9.02) * mm, v(-4.77, -8.93) * mm, v(-4.84, -8.91) * mm, v(-4.84, -8.98) * mm]});
            skFitSpline(sketch, "E260", {"points": [v(-4.84, -8.98) * mm, v(-4.84, -9.04) * mm, v(-5.03, -9.02) * mm, v(-5.26, -8.93) * mm]});
            skFitSpline(sketch, "E261", {"points": [v(-5.26, -8.93) * mm, v(-5.65, -8.78) * mm, v(-5.73, -8.85) * mm, v(-6.25, -9.71) * mm]});
            skFitSpline(sketch, "E262", {"points": [v(-6.25, -9.71) * mm, v(-7.48, -11.76) * mm, v(-7.92, -12.42) * mm, v(-8.72, -13.33) * mm]});
            skFitSpline(sketch, "E263", {"points": [v(-8.72, -13.33) * mm, v(-9.45, -14.15) * mm, v(-10.3, -14.8) * mm, v(-10.59, -14.75) * mm]});
            skFitSpline(sketch, "E264", {"points": [v(-10.59, -14.75) * mm, v(-10.64, -14.74) * mm, v(-10.9, -14.79) * mm, v(-11.19, -14.85) * mm]});
            skFitSpline(sketch, "E265", {"points": [v(-11.19, -14.85) * mm, v(-11.6, -14.94) * mm, v(-11.97, -15.37) * mm, v(-13.25, -17.3) * mm]});
            skFitSpline(sketch, "E266", {"points": [v(-13.25, -17.3) * mm, v(-15.87, -21.23) * mm, v(-16.95, -23.97) * mm, v(-17.15, -27.15) * mm]});
            skFitSpline(sketch, "E267", {"points": [v(-16.05, -28.52) * mm, v(-13.71, -28.62) * mm, v(-13.81, -28.66) * mm, v(-12.5, -27.26) * mm]});
            skFitSpline(sketch, "E268", {"points": [v(10.32, -22.75) * mm, v(12.14, -20.54) * mm, v(13.68, -18.92) * mm, v(14.03, -18.83) * mm]});
            skFitSpline(sketch, "E269", {"points": [v(14.03, -18.83) * mm, v(14.3, -18.76) * mm, v(14.68, -19.04) * mm, v(15.62, -20) * mm]});
            skFitSpline(sketch, "E270", {"points": [v(15.62, -20) * mm, v(16.81, -21.2) * mm, v(20.67, -23.92) * mm, v(22.12, -24.58) * mm]});
            skFitSpline(sketch, "E271", {"points": [v(24.01, -23.63) * mm, v(24.7, -22.95) * mm, v(25.6, -21.9) * mm, v(26, -21.3) * mm]});
            skFitSpline(sketch, "E272", {"points": [v(26, -21.3) * mm, v(26.98, -19.82) * mm, v(27.76, -17.35) * mm, v(27.87, -15.36) * mm]});
            skFitSpline(sketch, "E273", {"points": [v(27.27, -14.85) * mm, v(26.16, -16.49) * mm, v(24.77, -17.88) * mm, v(24.38, -17.74) * mm]});
            skFitSpline(sketch, "E274", {"points": [v(24.38, -17.74) * mm, v(23.58, -17.44) * mm, v(23.62, -16.79) * mm, v(24.5, -16) * mm]});
            skFitSpline(sketch, "E275", {"points": [v(24.5, -16) * mm, v(26.37, -14.32) * mm, v(28.53, -9.7) * mm, v(28.73, -6.91) * mm]});
            skFitSpline(sketch, "E276", {"points": [v(28.73, -6.91) * mm, v(28.78, -6.23) * mm, v(28.77, -5.67) * mm, v(28.71, -5.67) * mm]});
            skFitSpline(sketch, "E277", {"points": [v(28.71, -5.67) * mm, v(28.66, -5.67) * mm, v(28.17, -5.9) * mm, v(27.62, -6.18) * mm]});
            skFitSpline(sketch, "E278", {"points": [v(27.62, -6.18) * mm, v(25.89, -7.06) * mm, v(24.95, -7.44) * mm, v(21.83, -8.5) * mm]});
            skFitSpline(sketch, "E279", {"points": [v(21.83, -8.5) * mm, v(21.17, -8.72) * mm, v(20.44, -8.95) * mm, v(20.2, -9) * mm]});
            skFitSpline(sketch, "E280", {"points": [v(20.2, -9) * mm, v(19.97, -9.04) * mm, v(19.39, -9.16) * mm, v(18.92, -9.26) * mm]});
            skFitSpline(sketch, "E281", {"points": [v(18.92, -9.26) * mm, v(17.44, -9.57) * mm, v(17.07, -9.62) * mm, v(15.48, -9.71) * mm]});
            skFitSpline(sketch, "E282", {"points": [v(15.48, -9.71) * mm, v(12.77, -9.87) * mm, v(12.42, -9.94) * mm, v(11.11, -10.58) * mm]});
            skFitSpline(sketch, "E283", {"points": [v(11.11, -10.58) * mm, v(10.18, -11.05) * mm, v(9.5, -11.56) * mm, v(8.6, -12.47) * mm]});
            skFitSpline(sketch, "E284", {"points": [v(8.6, -12.47) * mm, v(6.63, -14.49) * mm, v(5.62, -16.8) * mm, v(5.62, -19.3) * mm]});
            skFitSpline(sketch, "E285", {"points": [v(5.62, -19.3) * mm, v(5.63, -21.38) * mm, v(6.2, -22.93) * mm, v(7.53, -24.44) * mm]});
            skFitSpline(sketch, "E286", {"points": [v(8.8, -24.62) * mm, v(9.08, -24.27) * mm, v(9.76, -23.42) * mm, v(10.32, -22.75) * mm]});
            skFitSpline(sketch, "E287", {"points": [v(-13.44, -13.47) * mm, v(-14.48, -11.67) * mm, v(-14.83, -10.4) * mm, v(-14.86, -8.39) * mm]});
            skFitSpline(sketch, "E288", {"points": [v(-14.86, -8.39) * mm, v(-14.87, -7.57) * mm, v(-14.92, -6.85) * mm, v(-14.98, -6.8) * mm]});
            skFitSpline(sketch, "E289", {"points": [v(-14.98, -6.8) * mm, v(-15.04, -6.73) * mm, v(-15.3, -6.65) * mm, v(-15.55, -6.6) * mm]});
            skFitSpline(sketch, "E290", {"points": [v(-15.55, -6.6) * mm, v(-16.69, -6.4) * mm, v(-19.62, -5.03) * mm, v(-20.36, -4.35) * mm]});
            skFitSpline(sketch, "E291", {"points": [v(-20.36, -4.35) * mm, v(-20.55, -4.18) * mm, v(-21.32, -3.53) * mm, v(-22.08, -2.9) * mm]});
            skFitSpline(sketch, "E292", {"points": [v(-22.08, -2.9) * mm, v(-23.53, -1.7) * mm, v(-24.23, -0.98) * mm, v(-24.56, -0.36) * mm]});
            skFitSpline(sketch, "E293", {"points": [v(-24.56, -0.36) * mm, v(-24.67, -0.15) * mm, v(-24.8, 0) * mm, v(-24.83, -0.04) * mm]});
            skFitSpline(sketch, "E294", {"points": [v(-24.83, -0.04) * mm, v(-25, -0.22) * mm, v(-25.14, -1.45) * mm, v(-25.13, -2.76) * mm]});
            skFitSpline(sketch, "E295", {"points": [v(-25.13, -2.76) * mm, v(-25.13, -4.44) * mm, v(-24.8, -5.4) * mm, v(-24.14, -5.7) * mm]});
            skFitSpline(sketch, "E296", {"points": [v(-24.14, -5.7) * mm, v(-23.87, -5.82) * mm, v(-23.7, -6.04) * mm, v(-23.7, -6.27) * mm]});
            skFitSpline(sketch, "E297", {"points": [v(-23.7, -6.27) * mm, v(-23.7, -6.94) * mm, v(-22.44, -8.46) * mm, v(-20.69, -9.9) * mm]});
            skFitSpline(sketch, "E298", {"points": [v(-20.69, -9.9) * mm, v(-20.27, -10.24) * mm, v(-19.93, -10.65) * mm, v(-19.93, -10.83) * mm]});
            skFitSpline(sketch, "E299", {"points": [v(-19.93, -10.83) * mm, v(-19.93, -11.22) * mm, v(-20.38, -11.67) * mm, v(-20.76, -11.67) * mm]});
            skFitSpline(sketch, "E300", {"points": [v(-20.76, -11.67) * mm, v(-21.1, -11.67) * mm, v(-23.04, -10.02) * mm, v(-23.74, -9.14) * mm]});
            skFitSpline(sketch, "E301", {"points": [v(-23.74, -9.14) * mm, v(-24, -8.81) * mm, v(-24.23, -8.65) * mm, v(-24.24, -8.78) * mm]});
            skFitSpline(sketch, "E302", {"points": [v(-24.24, -8.78) * mm, v(-24.5, -12.2) * mm, v(-23.28, -15.1) * mm, v(-20.68, -17.24) * mm]});
            skFitSpline(sketch, "E303", {"points": [v(-20.68, -17.24) * mm, v(-19.63, -18.1) * mm, v(-18.25, -18.89) * mm, v(-17.02, -19.32) * mm]});
            skFitSpline(sketch, "E304", {"points": [v(-15.4, -17.9) * mm, v(-14.82, -17) * mm, v(-14.04, -15.82) * mm, v(-13.66, -15.29) * mm]});
            skFitSpline(sketch, "E305", {"points": [v(2.02, -16.97) * mm, v(2.35, -16.77) * mm, v(2.8, -16.4) * mm, v(3.01, -16.15) * mm]});
            skFitSpline(sketch, "E306", {"points": [v(3.01, -16.15) * mm, v(3.58, -15.5) * mm, v(4.96, -12.56) * mm, v(5.2, -11.5) * mm]});
            skFitSpline(sketch, "E307", {"points": [v(5.2, -11.5) * mm, v(5.22, -11.36) * mm, v(5.4, -10.63) * mm, v(5.6, -9.87) * mm]});
            skFitSpline(sketch, "E308", {"points": [v(5.6, -9.87) * mm, v(5.78, -9.12) * mm, v(5.98, -8.2) * mm, v(6.03, -7.82) * mm]});
            skFitSpline(sketch, "E309", {"points": [v(6.03, -7.82) * mm, v(6.08, -7.44) * mm, v(6.16, -7.01) * mm, v(6.21, -6.87) * mm]});
            skFitSpline(sketch, "E310", {"points": [v(6.21, -6.87) * mm, v(6.3, -6.64) * mm, v(6.35, -6.14) * mm, v(6.56, -3.53) * mm]});
            skFitSpline(sketch, "E311", {"points": [v(6.56, -3.53) * mm, v(6.75, -1.01) * mm, v(6.63, -0.1) * mm, v(5.98, 0.97) * mm]});
            skFitSpline(sketch, "E312", {"points": [v(5.98, 0.97) * mm, v(5.26, 2.13) * mm, v(4.3, 2.36) * mm, v(2.64, 1.78) * mm]});
            skFitSpline(sketch, "E313", {"points": [v(2.64, 1.78) * mm, v(1.36, 1.33) * mm, v(0.85, 0.99) * mm, v(-0.45, -0.3) * mm]});
            skFitSpline(sketch, "E314", {"points": [v(-0.45, -0.3) * mm, v(-2.6, -2.42) * mm, v(-3.15, -4) * mm, v(-3.16, -7.9) * mm]});
            skFitSpline(sketch, "E315", {"points": [v(-3.16, -7.9) * mm, v(-3.17, -11.12) * mm, v(-2.24, -14.64) * mm, v(-0.93, -16.37) * mm]});
            skFitSpline(sketch, "E316", {"points": [v(-0.93, -16.37) * mm, v(-0.17, -17.37) * mm, v(0.98, -17.6) * mm, v(2.02, -16.97) * mm]});
            skFitSpline(sketch, "E317", {"points": [v(-9.85, -12.36) * mm, v(-9.4, -11.93) * mm, v(-7.9, -9.7) * mm, v(-7.3, -8.57) * mm]});
            skFitSpline(sketch, "E318", {"points": [v(-7.3, -8.57) * mm, v(-6.9, -7.82) * mm, v(-6.9, -7.76) * mm, v(-7.15, -7.05) * mm]});
            skFitSpline(sketch, "E319", {"points": [v(-7.15, -7.05) * mm, v(-7.5, -6.1) * mm, v(-7.28, -2.97) * mm, v(-6.81, -2.07) * mm]});
            skFitSpline(sketch, "E320", {"points": [v(-7.92, -0.7) * mm, v(-8.66, -0.21) * mm, v(-9.54, 0.45) * mm, v(-9.87, 0.76) * mm]});
            skFitSpline(sketch, "E321", {"points": [v(-9.87, 0.76) * mm, v(-10.42, 1.3) * mm, v(-10.48, 1.32) * mm, v(-10.7, 1.05) * mm]});
            skFitSpline(sketch, "E322", {"points": [v(-10.7, 1.05) * mm, v(-11.22, 0.44) * mm, v(-11.71, -0.59) * mm, v(-12.29, -2.28) * mm]});
            skFitSpline(sketch, "E323", {"points": [v(-12.29, -2.28) * mm, v(-13.04, -4.5) * mm, v(-13.36, -6.24) * mm, v(-13.4, -8.3) * mm]});
            skFitSpline(sketch, "E324", {"points": [v(-13.4, -8.3) * mm, v(-13.43, -9.86) * mm, v(-13.41, -9.96) * mm, v(-12.74, -11.38) * mm]});
            skFitSpline(sketch, "E325", {"points": [v(-12.74, -11.38) * mm, v(-11.8, -13.36) * mm, v(-11.14, -13.58) * mm, v(-9.85, -12.36) * mm]});
            skFitSpline(sketch, "E326", {"points": [v(8.67, -10.4) * mm, v(9.26, -9.96) * mm, v(9.74, -9.54) * mm, v(9.74, -9.46) * mm]});
            skFitSpline(sketch, "E327", {"points": [v(9.74, -9.46) * mm, v(9.74, -9.25) * mm, v(8.45, -7.32) * mm, v(8.14, -7.06) * mm]});
            skFitSpline(sketch, "E328", {"points": [v(8.14, -7.06) * mm, v(7.78, -6.77) * mm, v(7.74, -6.8) * mm, v(7.63, -7.56) * mm]});
            skFitSpline(sketch, "E329", {"points": [v(7.63, -7.56) * mm, v(7.57, -8.06) * mm, v(7.08, -10.05) * mm, v(6.54, -12.02) * mm]});
            skFitSpline(sketch, "E330", {"points": [v(6.54, -12.02) * mm, v(6.44, -12.41) * mm, v(6.47, -12.4) * mm, v(7.01, -11.83) * mm]});
            skFitSpline(sketch, "E331", {"points": [v(7.01, -11.83) * mm, v(7.33, -11.5) * mm, v(8.08, -10.86) * mm, v(8.67, -10.4) * mm]});
            skFitSpline(sketch, "E332", {"points": [v(-4.63, -6.91) * mm, v(-4.68, -6.6) * mm, v(-4.4, -4.74) * mm, v(-4.06, -3.18) * mm]});
            skFitSpline(sketch, "E333", {"points": [v(-4.06, -3.18) * mm, v(-3.97, -2.72) * mm, v(-4.02, -2.62) * mm, v(-4.4, -2.45) * mm]});
            skFitSpline(sketch, "E334", {"points": [v(-4.4, -2.45) * mm, v(-5.14, -2.11) * mm, v(-5.31, -2.2) * mm, v(-5.6, -3.07) * mm]});
            skFitSpline(sketch, "E335", {"points": [v(-5.6, -3.07) * mm, v(-5.9, -4) * mm, v(-5.98, -5.12) * mm, v(-5.79, -6.02) * mm]});
            skFitSpline(sketch, "E336", {"points": [v(-5.79, -6.02) * mm, v(-5.57, -7.04) * mm, v(-4.5, -7.87) * mm, v(-4.63, -6.91) * mm]});
            skFitSpline(sketch, "E337", {"points": [v(10.62, -1.64) * mm, v(11.22, -1.49) * mm, v(12.4, -1.03) * mm, v(13.26, -0.62) * mm]});
            skFitSpline(sketch, "E338", {"points": [v(13.26, -0.62) * mm, v(14.1, -0.22) * mm, v(15.3, 0.35) * mm, v(15.93, 0.65) * mm]});
            skFitSpline(sketch, "E339", {"points": [v(15.93, 0.65) * mm, v(18.2, 1.72) * mm, v(23.13, 5.93) * mm, v(25.38, 8.7) * mm]});
            skFitSpline(sketch, "E340", {"points": [v(25.38, 8.7) * mm, v(27.32, 11.12) * mm, v(28.93, 13.9) * mm, v(29.38, 15.62) * mm]});
            skFitSpline(sketch, "E341", {"points": [v(28.6, 17.81) * mm, v(28.03, 18.53) * mm, v(27.51, 19.2) * mm, v(27.44, 19.28) * mm]});
            skFitSpline(sketch, "E342", {"points": [v(27.44, 19.28) * mm, v(27.37, 19.38) * mm, v(27.07, 19.76) * mm, v(26.77, 20.13) * mm]});
            skFitSpline(sketch, "E343", {"points": [v(26.77, 20.13) * mm, v(26.47, 20.5) * mm, v(26.26, 20.87) * mm, v(26.31, 20.95) * mm]});
            skFitSpline(sketch, "E344", {"points": [v(26.31, 20.95) * mm, v(26.36, 21.03) * mm, v(26.33, 21.07) * mm, v(26.24, 21.05) * mm]});
            skFitSpline(sketch, "E345", {"points": [v(26.24, 21.05) * mm, v(26.15, 21.02) * mm, v(25.34, 21.85) * mm, v(24.45, 22.89) * mm]});
            skFitSpline(sketch, "E346", {"points": [v(24.45, 22.89) * mm, v(22.42, 25.24) * mm, v(21.47, 26.23) * mm, v(21.23, 26.23) * mm]});
            skFitSpline(sketch, "E347", {"points": [v(21.23, 26.23) * mm, v(20.8, 26.23) * mm, v(15.7, 24.7) * mm, v(14.54, 24.22) * mm]});
            skFitSpline(sketch, "E348", {"points": [v(14.54, 24.22) * mm, v(14.4, 24.16) * mm, v(14.23, 24.1) * mm, v(14.16, 24.08) * mm]});
            skFitSpline(sketch, "E349", {"points": [v(14.16, 24.08) * mm, v(14.08, 24.06) * mm, v(13.99, 24.02) * mm, v(13.94, 24) * mm]});
            skFitSpline(sketch, "E350", {"points": [v(13.94, 24) * mm, v(13.9, 23.98) * mm, v(13.8, 23.95) * mm, v(13.73, 23.94) * mm]});
            skFitSpline(sketch, "E351", {"points": [v(13.73, 23.94) * mm, v(13.62, 23.91) * mm, v(11.34, 23.12) * mm, v(10.6, 22.84) * mm]});
            skFitSpline(sketch, "E352", {"points": [v(10.6, 22.84) * mm, v(10.46, 22.8) * mm, v(10.26, 22.73) * mm, v(10.17, 22.7) * mm]});
            skFitSpline(sketch, "E353", {"points": [v(10.17, 22.7) * mm, v(10.07, 22.68) * mm, v(9.16, 22.3) * mm, v(8.14, 21.87) * mm]});
            skFitSpline(sketch, "E354", {"points": [v(8.14, 21.87) * mm, v(7.11, 21.44) * mm, v(6.14, 21.09) * mm, v(5.96, 21.09) * mm]});
            skFitSpline(sketch, "E355", {"points": [v(5.96, 21.09) * mm, v(5.79, 21.09) * mm, v(5.53, 20.97) * mm, v(5.39, 20.83) * mm]});
            skFitSpline(sketch, "E356", {"points": [v(5.39, 20.83) * mm, v(4.76, 20.2) * mm, v(4.2, 20.66) * mm, v(4.15, 21.86) * mm]});
            skFitSpline(sketch, "E357", {"points": [v(4.15, 21.86) * mm, v(4.12, 22.34) * mm, v(4.04, 22.8) * mm, v(3.84, 23.46) * mm]});
            skFitSpline(sketch, "E358", {"points": [v(3.84, 23.46) * mm, v(3.79, 23.62) * mm, v(3.71, 23.98) * mm, v(3.66, 24.26) * mm]});
            skFitSpline(sketch, "E359", {"points": [v(3.66, 24.26) * mm, v(2.9, 28.98) * mm, v(2.7, 29.88) * mm, v(2.14, 31.23) * mm]});
            skFitSpline(sketch, "E360", {"points": [v(1.17, 31.38) * mm, v(0.74, 31.21) * mm, v(-0.19, 30.95) * mm, v(-0.9, 30.79) * mm]});
            skFitSpline(sketch, "E361", {"points": [v(-0.9, 30.79) * mm, v(-2.23, 30.48) * mm, v(-7.85, 28.35) * mm, v(-8.83, 27.78) * mm]});
            skFitSpline(sketch, "E362", {"points": [v(-8.83, 27.78) * mm, v(-9.75, 27.23) * mm, v(-10.33, 27.48) * mm, v(-10.33, 28.43) * mm]});
            skFitSpline(sketch, "E363", {"points": [v(-10.33, 28.43) * mm, v(-10.34, 28.78) * mm, v(-10.41, 29.37) * mm, v(-10.5, 29.75) * mm]});
            skFitSpline(sketch, "E364", {"points": [v(-10.5, 29.75) * mm, v(-10.6, 30.12) * mm, v(-10.7, 30.55) * mm, v(-10.74, 30.7) * mm]});
            skFitSpline(sketch, "E365", {"points": [v(-10.74, 30.7) * mm, v(-10.78, 30.84) * mm, v(-11.06, 31.6) * mm, v(-11.38, 32.4) * mm]});
            skFitSpline(sketch, "E366", {"points": [v(-11.38, 32.4) * mm, v(-11.69, 33.2) * mm, v(-11.93, 33.92) * mm, v(-11.9, 34) * mm]});
            skFitSpline(sketch, "E367", {"points": [v(-11.9, 34) * mm, v(-11.72, 34.67) * mm, v(-13.2, 33.15) * mm, v(-14.7, 31.12) * mm]});
            skFitSpline(sketch, "E368", {"points": [v(-15.28, 29.52) * mm, v(-14.22, 29.42) * mm, v(-13.31, 27.88) * mm, v(-13.14, 25.87) * mm]});
            skFitSpline(sketch, "E369", {"points": [v(-13.14, 25.87) * mm, v(-13.1, 25.39) * mm, v(-13.03, 24.92) * mm, v(-12.97, 24.84) * mm]});
            skFitSpline(sketch, "E370", {"points": [v(-12.97, 24.84) * mm, v(-12.81, 24.57) * mm, v(-13.09, 23.66) * mm, v(-13.33, 23.66) * mm]});
            skFitSpline(sketch, "E371", {"points": [v(-13.33, 23.66) * mm, v(-13.6, 23.66) * mm, v(-13.76, 24.03) * mm, v(-13.76, 24.65) * mm]});
            skFitSpline(sketch, "E372", {"points": [v(-13.76, 24.65) * mm, v(-13.76, 24.89) * mm, v(-13.86, 25.21) * mm, v(-13.99, 25.36) * mm]});
            skFitSpline(sketch, "E373", {"points": [v(-13.99, 25.36) * mm, v(-14.11, 25.5) * mm, v(-14.3, 25.95) * mm, v(-14.42, 26.35) * mm]});
            skFitSpline(sketch, "E374", {"points": [v(-14.42, 26.35) * mm, v(-14.68, 27.28) * mm, v(-15.39, 27.87) * mm, v(-15.86, 27.56) * mm]});
            skFitSpline(sketch, "E375", {"points": [v(-15.86, 27.56) * mm, v(-16.04, 27.44) * mm, v(-16.18, 27.27) * mm, v(-16.18, 27.17) * mm]});
            skFitSpline(sketch, "E376", {"points": [v(-16.18, 27.17) * mm, v(-16.18, 26.92) * mm, v(-16.7, 26.4) * mm, v(-16.95, 26.4) * mm]});
            skFitSpline(sketch, "E377", {"points": [v(-16.95, 26.4) * mm, v(-17.15, 26.4) * mm, v(-17.6, 25.78) * mm, v(-17.58, 25.55) * mm]});
            skFitSpline(sketch, "E378", {"points": [v(-17.58, 25.55) * mm, v(-17.58, 25.5) * mm, v(-17.6, 25.38) * mm, v(-17.64, 25.29) * mm]});
            skFitSpline(sketch, "E379", {"points": [v(-17.64, 25.29) * mm, v(-18.2, 23.8) * mm, v(-18.6, 19.14) * mm, v(-18.24, 18.54) * mm]});
            skFitSpline(sketch, "E380", {"points": [v(-18.24, 18.54) * mm, v(-18.14, 18.38) * mm, v(-17.7, 18.38) * mm, v(-16.34, 18.53) * mm]});
            skFitSpline(sketch, "E381", {"points": [v(-16.34, 18.53) * mm, v(-14.69, 18.7) * mm, v(-14.55, 18.7) * mm, v(-14.12, 18.39) * mm]});
            skFitSpline(sketch, "E382", {"points": [v(-14.12, 18.39) * mm, v(-13.88, 18.2) * mm, v(-13.6, 17.9) * mm, v(-13.5, 17.72) * mm]});
            skFitSpline(sketch, "E383", {"points": [v(-13.5, 17.72) * mm, v(-12.06, 14.95) * mm, v(-9.61, 12.87) * mm, v(-6.87, 12.09) * mm]});
            skFitSpline(sketch, "E384", {"points": [v(-6.87, 12.09) * mm, v(-5.8, 11.78) * mm, v(-5.59, 11.6) * mm, v(-5.36, 10.81) * mm]});
            skFitSpline(sketch, "E385", {"points": [v(-5.36, 10.81) * mm, v(-5.2, 10.25) * mm, v(-5.43, 9.86) * mm, v(-7.1, 7.86) * mm]});
            skFitSpline(sketch, "E386", {"points": [v(-7.1, 7.86) * mm, v(-8.63, 6.04) * mm, v(-10.16, 3.86) * mm, v(-10.15, 3.5) * mm]});
            skFitSpline(sketch, "E387", {"points": [v(-10.15, 3.5) * mm, v(-10.15, 3.23) * mm, v(-8.95, 2) * mm, v(-7.92, 1.24) * mm]});
            skFitSpline(sketch, "E388", {"points": [v(-7.92, 1.24) * mm, v(-6.94, 0.51) * mm, v(-5.48, -0.27) * mm, v(-4.13, -0.77) * mm]});
            skFitSpline(sketch, "E389", {"points": [v(-1.73, 0.55) * mm, v(0, 2.3) * mm, v(1.24, 3.05) * mm, v(3.02, 3.43) * mm]});
            skFitSpline(sketch, "E390", {"points": [v(3.02, 3.43) * mm, v(5.87, 4.04) * mm, v(7.65, 2.7) * mm, v(7.94, -0.28) * mm]});
            skFitSpline(sketch, "E391", {"points": [v(7.94, -0.28) * mm, v(8.12, -2.09) * mm, v(8.11, -2.06) * mm, v(8.87, -1.98) * mm]});
            skFitSpline(sketch, "E392", {"points": [v(8.87, -1.98) * mm, v(9.23, -1.95) * mm, v(10.03, -1.8) * mm, v(10.62, -1.64) * mm]});
            skFitSpline(sketch, "E393", {"points": [v(4.27, 9.75) * mm, v(4.1, 9.86) * mm, v(4.02, 10.32) * mm, v(4, 11.35) * mm]});
            skFitSpline(sketch, "E394", {"points": [v(4, 11.35) * mm, v(3.98, 12.39) * mm, v(3.89, 12.9) * mm, v(3.68, 13.2) * mm]});
            skFitSpline(sketch, "E395", {"points": [v(3.68, 13.2) * mm, v(3.52, 13.43) * mm, v(3.4, 13.81) * mm, v(3.4, 14.05) * mm]});
            skFitSpline(sketch, "E396", {"points": [v(3.4, 14.05) * mm, v(3.4, 15) * mm, v(2.3, 16.17) * mm, v(1.81, 15.73) * mm]});
            skFitSpline(sketch, "E397", {"points": [v(1.81, 15.73) * mm, v(1.15, 15.12) * mm, v(-0.91, 14.33) * mm, v(-1.42, 14.48) * mm]});
            skFitSpline(sketch, "E398", {"points": [v(-1.42, 14.48) * mm, v(-1.69, 14.57) * mm, v(-1.76, 14.72) * mm, v(-1.72, 15.1) * mm]});
            skFitSpline(sketch, "E399", {"points": [v(-1.72, 15.1) * mm, v(-1.67, 15.55) * mm, v(-1.54, 15.67) * mm, v(-0.65, 16.03) * mm]});
            skFitSpline(sketch, "E400", {"points": [v(-0.65, 16.03) * mm, v(-0.09, 16.26) * mm, v(0.7, 16.68) * mm, v(1.11, 16.98) * mm]});
            skFitSpline(sketch, "E401", {"points": [v(1.11, 16.98) * mm, v(1.76, 17.44) * mm, v(1.96, 17.5) * mm, v(2.58, 17.41) * mm]});
            skFitSpline(sketch, "E402", {"points": [v(2.58, 17.41) * mm, v(3.43, 17.3) * mm, v(3.87, 16.84) * mm, v(4.62, 15.3) * mm]});
            skFitSpline(sketch, "E403", {"points": [v(4.62, 15.3) * mm, v(5.1, 14.3) * mm, v(5.19, 14.22) * mm, v(5.85, 14.1) * mm]});
            skFitSpline(sketch, "E404", {"points": [v(5.85, 14.1) * mm, v(6.82, 13.93) * mm, v(7.9, 14) * mm, v(8.93, 14.3) * mm]});
            skFitSpline(sketch, "E405", {"points": [v(8.93, 14.3) * mm, v(9.88, 14.59) * mm, v(12.77, 16.08) * mm, v(13.63, 16.73) * mm]});
            skFitSpline(sketch, "E406", {"points": [v(13.63, 16.73) * mm, v(13.93, 16.96) * mm, v(14.3, 17.14) * mm, v(14.46, 17.14) * mm]});
            skFitSpline(sketch, "E407", {"points": [v(14.46, 17.14) * mm, v(14.68, 17.14) * mm, v(14.63, 16.94) * mm, v(14.17, 16.1) * mm]});
            skFitSpline(sketch, "E408", {"points": [v(14.17, 16.1) * mm, v(13.62, 15.09) * mm, v(13.54, 15.02) * mm, v(11.88, 14.18) * mm]});
            skFitSpline(sketch, "E409", {"points": [v(11.88, 14.18) * mm, v(9.73, 13.1) * mm, v(8.62, 12.72) * mm, v(7.22, 12.57) * mm]});
            skFitSpline(sketch, "E410", {"points": [v(6.76, 12.23) * mm, v(7.13, 12.1) * mm, v(7.77, 11.95) * mm, v(8.2, 11.9) * mm]});
            skFitSpline(sketch, "E411", {"points": [v(8.2, 11.9) * mm, v(8.62, 11.83) * mm, v(9.01, 11.76) * mm, v(9.07, 11.73) * mm]});
            skFitSpline(sketch, "E412", {"points": [v(9.07, 11.73) * mm, v(9.35, 11.56) * mm, v(11.61, 12.06) * mm, v(12.25, 12.43) * mm]});
            skFitSpline(sketch, "E413", {"points": [v(12.25, 12.43) * mm, v(13.28, 13.03) * mm, v(13.47, 12.95) * mm, v(12.8, 12.2) * mm]});
            skFitSpline(sketch, "E414", {"points": [v(12.8, 12.2) * mm, v(12.49, 11.85) * mm, v(12.04, 11.32) * mm, v(11.8, 11.02) * mm]});
            skFitSpline(sketch, "E415", {"points": [v(9.4, 10.47) * mm, v(8.18, 10.46) * mm, v(7.08, 10.54) * mm, v(6.52, 10.7) * mm]});
            skFitSpline(sketch, "E416", {"points": [v(6.52, 10.7) * mm, v(6.03, 10.83) * mm, v(5.62, 10.92) * mm, v(5.6, 10.9) * mm]});
            skFitSpline(sketch, "E417", {"points": [v(5.6, 10.9) * mm, v(5.6, 10.9) * mm, v(5.56, 10.7) * mm, v(5.52, 10.46) * mm]});
            skFitSpline(sketch, "E418", {"points": [v(5.52, 10.46) * mm, v(5.38, 9.68) * mm, v(4.85, 9.38) * mm, v(4.27, 9.75) * mm]});
            skFitSpline(sketch, "E419", {"points": [v(-13.22, 2.18) * mm, v(-12.98, 2.44) * mm, v(-12.6, 2.96) * mm, v(-12.38, 3.33) * mm]});
            skFitSpline(sketch, "E420", {"points": [v(-12.38, 3.33) * mm, v(-12.16, 3.71) * mm, v(-11.53, 4.6) * mm, v(-10.97, 5.3) * mm]});
            skFitSpline(sketch, "E421", {"points": [v(-10.97, 5.3) * mm, v(-8.5, 8.45) * mm, v(-7.08, 10.4) * mm, v(-7.2, 10.52) * mm]});
            skFitSpline(sketch, "E422", {"points": [v(-7.2, 10.52) * mm, v(-7.41, 10.74) * mm, v(-7.72, 10.6) * mm, v(-7.65, 10.32) * mm]});
            skFitSpline(sketch, "E423", {"points": [v(-7.65, 10.32) * mm, v(-7.56, 9.93) * mm, v(-7.8, 9.65) * mm, v(-9.02, 8.7) * mm]});
            skFitSpline(sketch, "E424", {"points": [v(-9.02, 8.7) * mm, v(-9.58, 8.26) * mm, v(-10.36, 7.44) * mm, v(-10.76, 6.87) * mm]});
            skFitSpline(sketch, "E425", {"points": [v(-10.76, 6.87) * mm, v(-11.15, 6.3) * mm, v(-11.54, 5.89) * mm, v(-11.62, 5.95) * mm]});
            skFitSpline(sketch, "E426", {"points": [v(-11.62, 5.95) * mm, v(-11.7, 6.02) * mm, v(-11.7, 6) * mm, v(-11.65, 5.88) * mm]});
            skFitSpline(sketch, "E427", {"points": [v(-11.65, 5.88) * mm, v(-11.58, 5.78) * mm, v(-11.76, 5.4) * mm, v(-12.02, 5.03) * mm]});
            skFitSpline(sketch, "E428", {"points": [v(-12.02, 5.03) * mm, v(-13.21, 3.4) * mm, v(-13.97, 3.24) * mm, v(-14.57, 4.44) * mm]});
            skFitSpline(sketch, "E429", {"points": [v(-14.57, 4.44) * mm, v(-14.99, 5.27) * mm, v(-15.05, 5.22) * mm, v(-14.8, 4.28) * mm]});
            skFitSpline(sketch, "E430", {"points": [v(-14.8, 4.28) * mm, v(-14.71, 3.95) * mm, v(-14.6, 3.4) * mm, v(-14.57, 3.07) * mm]});
            skFitSpline(sketch, "E431", {"points": [v(-14.57, 3.07) * mm, v(-14.47, 2.31) * mm, v(-14.16, 1.7) * mm, v(-13.87, 1.7) * mm]});
            skFitSpline(sketch, "E432", {"points": [v(-13.87, 1.7) * mm, v(-13.75, 1.7) * mm, v(-13.46, 1.92) * mm, v(-13.22, 2.18) * mm]});
            skFitSpline(sketch, "E433", {"points": [v(-11.36, 8.78) * mm, v(-11.36, 8.85) * mm, v(-11.94, 8.96) * mm, v(-13.63, 9.18) * mm]});
            skFitSpline(sketch, "E434", {"points": [v(-13.63, 9.18) * mm, v(-14.08, 9.24) * mm, v(-14.1, 9.21) * mm, v(-14.1, 8.52) * mm]});
            skFitSpline(sketch, "E435", {"points": [v(-14.1, 8.52) * mm, v(-14.1, 7.82) * mm, v(-13.75, 6.22) * mm, v(-13.51, 5.84) * mm]});
            skFitSpline(sketch, "E436", {"points": [v(-13.51, 5.84) * mm, v(-13.42, 5.69) * mm, v(-11.36, 8.5) * mm, v(-11.36, 8.78) * mm]});
            skFitSpline(sketch, "E437", {"points": [v(-9.36, 11.3) * mm, v(-9.8, 11.51) * mm, v(-10.26, 11.78) * mm, v(-10.38, 11.89) * mm]});
            skFitSpline(sketch, "E438", {"points": [v(-10.38, 11.89) * mm, v(-10.5, 12) * mm, v(-10.93, 12.35) * mm, v(-11.36, 12.67) * mm]});
            skFitSpline(sketch, "E439", {"points": [v(-11.36, 12.67) * mm, v(-12.79, 13.75) * mm, v(-13.78, 14.82) * mm, v(-14.29, 15.8) * mm]});
            skFitSpline(sketch, "E440", {"points": [v(-14.29, 15.8) * mm, v(-14.84, 16.9) * mm, v(-15.18, 17.15) * mm, v(-15.92, 17.06) * mm]});
            skFitSpline(sketch, "E441", {"points": [v(-15.92, 17.06) * mm, v(-16.2, 17.03) * mm, v(-16.92, 16.95) * mm, v(-17.53, 16.89) * mm]});
            skFitSpline(sketch, "E442", {"points": [v(-17.53, 16.89) * mm, v(-18.15, 16.83) * mm, v(-18.92, 16.7) * mm, v(-19.25, 16.62) * mm]});
            skFitSpline(sketch, "E443", {"points": [v(-19.25, 16.62) * mm, v(-19.58, 16.54) * mm, v(-20.12, 16.42) * mm, v(-20.45, 16.37) * mm]});
            skFitSpline(sketch, "E444", {"points": [v(-20.45, 16.37) * mm, v(-20.78, 16.32) * mm, v(-21.16, 16.24) * mm, v(-21.3, 16.2) * mm]});
            skFitSpline(sketch, "E445", {"points": [v(-21.3, 16.2) * mm, v(-21.45, 16.15) * mm, v(-21.86, 16.08) * mm, v(-22.22, 16.04) * mm]});
            skFitSpline(sketch, "E446", {"points": [v(-22.22, 16.04) * mm, v(-22.59, 16) * mm, v(-22.92, 15.92) * mm, v(-22.97, 15.88) * mm]});
            skFitSpline(sketch, "E447", {"points": [v(-22.97, 15.88) * mm, v(-23.24, 15.6) * mm, v(-19.86, 13.17) * mm, v(-17.7, 12.08) * mm]});
            skFitSpline(sketch, "E448", {"points": [v(-17.7, 12.08) * mm, v(-15.05, 10.74) * mm, v(-11.24, 10.1) * mm, v(-9.31, 10.68) * mm]});
            skFitSpline(sketch, "E449", {"points": [v(35.05, 16.2) * mm, v(35.09, 17.8) * mm, v(35.18, 19.77) * mm, v(35.25, 20.57) * mm]});
            skFitSpline(sketch, "E450", {"points": [v(35.25, 20.57) * mm, v(35.44, 22.62) * mm, v(35.3, 30.88) * mm, v(35.04, 33.52) * mm]});
            skFitSpline(sketch, "E451", {"points": [v(35.04, 33.52) * mm, v(34.9, 34.8) * mm, v(34.67, 36.6) * mm, v(34.41, 38.24) * mm]});
            skFitSpline(sketch, "E452", {"points": [v(34.41, 38.24) * mm, v(34.32, 38.85) * mm, v(34.2, 39.58) * mm, v(34.17, 39.87) * mm]});
            skFitSpline(sketch, "E453", {"points": [v(34.17, 39.87) * mm, v(34.13, 40.15) * mm, v(34.06, 40.6) * mm, v(34, 40.85) * mm]});
            skFitSpline(sketch, "E454", {"points": [v(34, 40.85) * mm, v(33.94, 41.1) * mm, v(33.9, 41.38) * mm, v(33.89, 41.45) * mm]});
            skFitSpline(sketch, "E455", {"points": [v(33.89, 41.45) * mm, v(33.88, 41.52) * mm, v(33.81, 41.76) * mm, v(33.73, 41.98) * mm]});
            skFitSpline(sketch, "E456", {"points": [v(33.73, 41.98) * mm, v(33.65, 42.2) * mm, v(33.54, 42.62) * mm, v(33.49, 42.92) * mm]});
            skFitSpline(sketch, "E457", {"points": [v(33.49, 42.92) * mm, v(33.1, 45.1) * mm, v(31.48, 49.44) * mm, v(30.11, 51.96) * mm]});
            skFitSpline(sketch, "E458", {"points": [v(30.11, 51.96) * mm, v(29.73, 52.67) * mm, v(29.15, 53.74) * mm, v(28.83, 54.33) * mm]});
            skFitSpline(sketch, "E459", {"points": [v(28.83, 54.33) * mm, v(27.87, 56.13) * mm, v(27.4, 56.8) * mm, v(26.3, 57.94) * mm]});
            skFitSpline(sketch, "E460", {"points": [v(26.3, 57.94) * mm, v(25.19, 59.1) * mm, v(23.19, 60.7) * mm, v(21.9, 61.45) * mm]});
            skFitSpline(sketch, "E461", {"points": [v(21.9, 61.45) * mm, v(21.22, 61.85) * mm, v(19.13, 62.66) * mm, v(18.31, 62.85) * mm]});
            skFitSpline(sketch, "E462", {"points": [v(18.31, 62.85) * mm, v(18.17, 62.88) * mm, v(17.83, 63) * mm, v(17.54, 63.1) * mm]});
            skFitSpline(sketch, "E463", {"points": [v(17.54, 63.1) * mm, v(16.6, 63.47) * mm, v(16.36, 63.5) * mm, v(13.68, 63.54) * mm]});
            skFitSpline(sketch, "E464", {"points": [v(13.68, 63.54) * mm, v(11.65, 63.57) * mm, v(10.66, 63.5) * mm, v(9.48, 63.26) * mm]});
            skFitSpline(sketch, "E465", {"points": [v(9.48, 63.26) * mm, v(8.63, 63.09) * mm, v(7.71, 62.9) * mm, v(7.44, 62.85) * mm]});
            skFitSpline(sketch, "E466", {"points": [v(7.44, 62.85) * mm, v(7.16, 62.8) * mm, v(6.87, 62.7) * mm, v(6.8, 62.66) * mm]});
            skFitSpline(sketch, "E467", {"points": [v(6.8, 62.66) * mm, v(6.72, 62.61) * mm, v(6.52, 62.55) * mm, v(6.35, 62.51) * mm]});
            skFitSpline(sketch, "E468", {"points": [v(6.35, 62.51) * mm, v(4.85, 62.2) * mm, v(1.56, 60.6) * mm, v(-0.84, 59) * mm]});
            skFitSpline(sketch, "E469", {"points": [v(-0.84, 59) * mm, v(-5.36, 56.01) * mm, v(-8.72, 53.05) * mm, v(-14.83, 46.65) * mm]});
            skFitSpline(sketch, "E470", {"points": [v(-14.83, 46.65) * mm, v(-16.6, 44.8) * mm, v(-18.78, 41.8) * mm, v(-20.1, 39.4) * mm]});
            skFitSpline(sketch, "E471", {"points": [v(-20.1, 39.4) * mm, v(-20.71, 38.27) * mm, v(-20.69, 38.25) * mm, v(-19.1, 38.66) * mm]});
            skFitSpline(sketch, "E472", {"points": [v(-19.1, 38.66) * mm, v(-18.57, 38.8) * mm, v(-17.86, 38.95) * mm, v(-17.53, 39) * mm]});
            skFitSpline(sketch, "E473", {"points": [v(-17.53, 39) * mm, v(-17.2, 39.06) * mm, v(-16.74, 39.13) * mm, v(-16.5, 39.18) * mm]});
            skFitSpline(sketch, "E474", {"points": [v(-16.5, 39.18) * mm, v(-16.27, 39.22) * mm, v(-15.7, 39.3) * mm, v(-15.23, 39.35) * mm]});
            skFitSpline(sketch, "E475", {"points": [v(-15.23, 39.35) * mm, v(-14.76, 39.4) * mm, v(-14.32, 39.5) * mm, v(-14.24, 39.55) * mm]});
            skFitSpline(sketch, "E476", {"points": [v(-14.24, 39.55) * mm, v(-14.16, 39.6) * mm, v(-13.71, 39.68) * mm, v(-13.25, 39.73) * mm]});
            skFitSpline(sketch, "E477", {"points": [v(-13.25, 39.73) * mm, v(-12.52, 39.8) * mm, v(-12.4, 39.77) * mm, v(-12.22, 39.44) * mm]});
            skFitSpline(sketch, "E478", {"points": [v(-12.22, 39.44) * mm, v(-12.1, 39.24) * mm, v(-12, 38.94) * mm, v(-11.96, 38.78) * mm]});
            skFitSpline(sketch, "E479", {"points": [v(-11.96, 38.78) * mm, v(-11.93, 38.62) * mm, v(-11.66, 37.8) * mm, v(-11.36, 36.95) * mm]});
            skFitSpline(sketch, "E480", {"points": [v(-11.36, 36.95) * mm, v(-11.06, 36.1) * mm, v(-10.79, 35.3) * mm, v(-10.75, 35.15) * mm]});
            skFitSpline(sketch, "E481", {"points": [v(-10.75, 35.15) * mm, v(-10.71, 35) * mm, v(-10.37, 33.98) * mm, v(-9.99, 32.87) * mm]});
            skFitSpline(sketch, "E482", {"points": [v(-9.99, 32.87) * mm, v(-9.6, 31.75) * mm, v(-9.3, 30.67) * mm, v(-9.3, 30.47) * mm]});
            skFitSpline(sketch, "E483", {"points": [v(-9.3, 30.47) * mm, v(-9.3, 30.26) * mm, v(-9.22, 29.98) * mm, v(-9.14, 29.84) * mm]});
            skFitSpline(sketch, "E484", {"points": [v(-9.14, 29.84) * mm, v(-8.94, 29.54) * mm, v(-8.28, 29.72) * mm, v(-4.52, 31.1) * mm]});
            skFitSpline(sketch, "E485", {"points": [v(-4.52, 31.1) * mm, v(-3.08, 31.64) * mm, v(-1.57, 32.15) * mm, v(-1.18, 32.23) * mm]});
            skFitSpline(sketch, "E486", {"points": [v(-1.18, 32.23) * mm, v(0.08, 32.5) * mm, v(0.21, 32.53) * mm, v(1.2, 33.02) * mm]});
            skFitSpline(sketch, "E487", {"points": [v(1.2, 33.02) * mm, v(2.6, 33.71) * mm, v(2.96, 33.55) * mm, v(3.49, 31.98) * mm]});
            skFitSpline(sketch, "E488", {"points": [v(3.49, 31.98) * mm, v(3.7, 31.32) * mm, v(3.93, 30.48) * mm, v(3.98, 30.12) * mm]});
            skFitSpline(sketch, "E489", {"points": [v(3.98, 30.12) * mm, v(4.03, 29.76) * mm, v(4.1, 29.41) * mm, v(4.15, 29.34) * mm]});
            skFitSpline(sketch, "E490", {"points": [v(4.15, 29.34) * mm, v(4.2, 29.27) * mm, v(4.28, 28.83) * mm, v(4.34, 28.36) * mm]});
            skFitSpline(sketch, "E491", {"points": [v(4.34, 28.36) * mm, v(4.4, 27.9) * mm, v(4.5, 27.2) * mm, v(4.58, 26.83) * mm]});
            skFitSpline(sketch, "E492", {"points": [v(4.58, 26.83) * mm, v(4.64, 26.45) * mm, v(4.7, 25.95) * mm, v(4.69, 25.72) * mm]});
            skFitSpline(sketch, "E493", {"points": [v(4.69, 25.72) * mm, v(4.68, 25.48) * mm, v(4.72, 25.25) * mm, v(4.77, 25.2) * mm]});
            skFitSpline(sketch, "E494", {"points": [v(4.77, 25.2) * mm, v(4.82, 25.15) * mm, v(5.01, 24.58) * mm, v(5.2, 23.92) * mm]});
            skFitSpline(sketch, "E495", {"points": [v(5.2, 23.92) * mm, v(5.52, 22.78) * mm, v(5.57, 22.71) * mm, v(6.05, 22.7) * mm]});
            skFitSpline(sketch, "E496", {"points": [v(6.05, 22.7) * mm, v(6.58, 22.69) * mm, v(8.46, 23.32) * mm, v(11.2, 24.43) * mm]});
            skFitSpline(sketch, "E497", {"points": [v(11.2, 24.43) * mm, v(12.05, 24.77) * mm, v(12.82, 25.07) * mm, v(12.91, 25.09) * mm]});
            skFitSpline(sketch, "E498", {"points": [v(12.91, 25.09) * mm, v(13, 25.1) * mm, v(13.17, 25.18) * mm, v(13.28, 25.25) * mm]});
            skFitSpline(sketch, "E499", {"points": [v(13.28, 25.25) * mm, v(13.38, 25.31) * mm, v(13.77, 25.42) * mm, v(14.14, 25.47) * mm]});
            skFitSpline(sketch, "E500", {"points": [v(14.14, 25.47) * mm, v(14.5, 25.53) * mm, v(14.93, 25.65) * mm, v(15.1, 25.74) * mm]});
            skFitSpline(sketch, "E501", {"points": [v(15.1, 25.74) * mm, v(15.26, 25.83) * mm, v(15.4, 25.87) * mm, v(15.4, 25.83) * mm]});
            skFitSpline(sketch, "E502", {"points": [v(15.4, 25.83) * mm, v(15.4, 25.79) * mm, v(16.11, 26.02) * mm, v(16.99, 26.35) * mm]});
            skFitSpline(sketch, "E503", {"points": [v(16.99, 26.35) * mm, v(17.86, 26.67) * mm, v(18.7, 26.97) * mm, v(18.85, 27) * mm]});
            skFitSpline(sketch, "E504", {"points": [v(18.85, 27) * mm, v(19, 27.03) * mm, v(19.63, 27.26) * mm, v(20.24, 27.5) * mm]});
            skFitSpline(sketch, "E505", {"points": [v(20.24, 27.5) * mm, v(21.54, 28.03) * mm, v(22.23, 28.07) * mm, v(22.38, 27.65) * mm]});
            skFitSpline(sketch, "E506", {"points": [v(22.38, 27.65) * mm, v(22.5, 27.3) * mm, v(23.33, 26.25) * mm, v(24.26, 25.28) * mm]});
            skFitSpline(sketch, "E507", {"points": [v(24.26, 25.28) * mm, v(24.62, 24.9) * mm, v(25.84, 23.43) * mm, v(26.97, 22.02) * mm]});
            skFitSpline(sketch, "E508", {"points": [v(26.97, 22.02) * mm, v(28.1, 20.61) * mm, v(29.3, 19.14) * mm, v(29.63, 18.76) * mm]});
            skFitSpline(sketch, "E509", {"points": [v(29.63, 18.76) * mm, v(29.96, 18.37) * mm, v(30.74, 17.45) * mm, v(31.35, 16.7) * mm]});
            skFitSpline(sketch, "E510", {"points": [v(31.35, 16.7) * mm, v(31.96, 15.95) * mm, v(32.56, 15.24) * mm, v(32.67, 15.12) * mm]});
            skFitSpline(sketch, "E511", {"points": [v(32.67, 15.12) * mm, v(32.78, 15) * mm, v(33.28, 14.36) * mm, v(33.78, 13.7) * mm]});
            skFitSpline(sketch, "E512", {"points": [v(33.78, 13.7) * mm, v(34.62, 12.55) * mm, v(34.69, 12.5) * mm, v(34.83, 12.88) * mm]});
            skFitSpline(sketch, "E513", {"points": [v(34.83, 12.88) * mm, v(34.91, 13.1) * mm, v(35, 14.6) * mm, v(35.05, 16.2) * mm]});
            skSolve(sketch);
        }
        {
            var Q0;
            Q0=makeQuery(id+"F0.imprint","IMPRINT",FACE,{"disambiguationData":[TD([[makeQuery(id+"F0.imprint","IMPRINT",EDGE,{"derivedFrom":sQuery(id+"F0.wireOp",EDGE,"E0")}),-1.0]])]});
            var Q1;
            Q1=makeQuery(id+"F0.imprint","IMPRINT",FACE,{"disambiguationData":[TD([[makeQuery(id+"F0.imprint","IMPRINT",EDGE,{"derivedFrom":sQuery(id+"F0.wireOp",EDGE,"E449")}),1.0]])]});
            var Q2;
            Q2=makeQuery(id+"F0.imprint","IMPRINT",FACE,{"disambiguationData":[TD([[makeQuery(id+"F0.imprint","IMPRINT",EDGE,{"derivedFrom":sQuery(id+"F0.wireOp",EDGE,"E38")}),1.0]])]});
            var Q3;
            Q3=makeQuery(id+"F0.imprint","IMPRINT",FACE,{"disambiguationData":[TD([[makeQuery(id+"F0.imprint","IMPRINT",EDGE,{"derivedFrom":sQuery(id+"F0.wireOp",EDGE,"E433")}),1.0]])]});
            var Q4;
            Q4=makeQuery(id+"F0.imprint","IMPRINT",FACE,{"disambiguationData":[TD([[makeQuery(id+"F0.imprint","IMPRINT",EDGE,{"derivedFrom":sQuery(id+"F0.wireOp",EDGE,"E419")}),1.0]])]});
            var Q5;
            Q5=makeQuery(id+"F0.imprint","IMPRINT",FACE,{"disambiguationData":[TD([[makeQuery(id+"F0.imprint","IMPRINT",EDGE,{"derivedFrom":sQuery(id+"F0.wireOp",EDGE,"E34")}),-1.0]])]});
            var Q6;
            Q6=makeQuery(id+"F0.imprint","IMPRINT",FACE,{"disambiguationData":[TD([[makeQuery(id+"F0.imprint","IMPRINT",EDGE,{"derivedFrom":sQuery(id+"F0.wireOp",EDGE,"E25")}),1.0]])]});
            var Q7;
            Q7=makeQuery(id+"F0.imprint","IMPRINT",FACE,{"disambiguationData":[TD([[makeQuery(id+"F0.imprint","IMPRINT",EDGE,{"derivedFrom":sQuery(id+"F0.wireOp",EDGE,"E19")}),1.0]])]});
            var Q8;
            Q8=makeQuery(id+"F0.imprint","IMPRINT",FACE,{"disambiguationData":[TD([[makeQuery(id+"F0.imprint","IMPRINT",EDGE,{"derivedFrom":sQuery(id+"F0.wireOp",EDGE,"E11")}),1.0]])]});
            var Q9;
            Q9=makeQuery(id+"F0.imprint","IMPRINT",FACE,{"disambiguationData":[TD([[makeQuery(id+"F0.imprint","IMPRINT",EDGE,{"derivedFrom":sQuery(id+"F0.wireOp",EDGE,"E326")}),1.0]])]});
            var Q10;
            Q10=makeQuery(id+"F0.imprint","IMPRINT",FACE,{"disambiguationData":[TD([[makeQuery(id+"F0.imprint","IMPRINT",EDGE,{"derivedFrom":sQuery(id+"F0.wireOp",EDGE,"E13")}),1.0]])]});
            var Q11;
            Q11=makeQuery(id+"F0.imprint","IMPRINT",FACE,{"disambiguationData":[TD([[makeQuery(id+"F0.imprint","IMPRINT",EDGE,{"derivedFrom":sQuery(id+"F0.wireOp",EDGE,"E5")}),1.0]])]});
            extrude(context, id + "F1", {"entities" : qUnion([Q0, Q1, Q2, Q3, Q4, Q5, Q6, Q7, Q8, Q9, Q10, Q11]), "depth" : 1 * mm, "offsetDistance" : 25 * mm});
        }
        {
            var Q0;
            Q0 = qSketchRegion(id + "F0", true);
            var Q1;
            Q1=makeQuery(id+"F0.imprint","IMPRINT",FACE,{"disambiguationData":[TD([[makeQuery(id+"F0.imprint","IMPRINT",EDGE,{"derivedFrom":sQuery(id+"F0.wireOp",EDGE,"E34")}),-1.0]])]});
            extrude(context, id + "F2", {"entities" : qUnion([Q0, Q1]), "operationType" : NewBodyOperationType.ADD, "depth" : 2 * mm, "offsetDistance" : 25 * mm});
        }
    });
